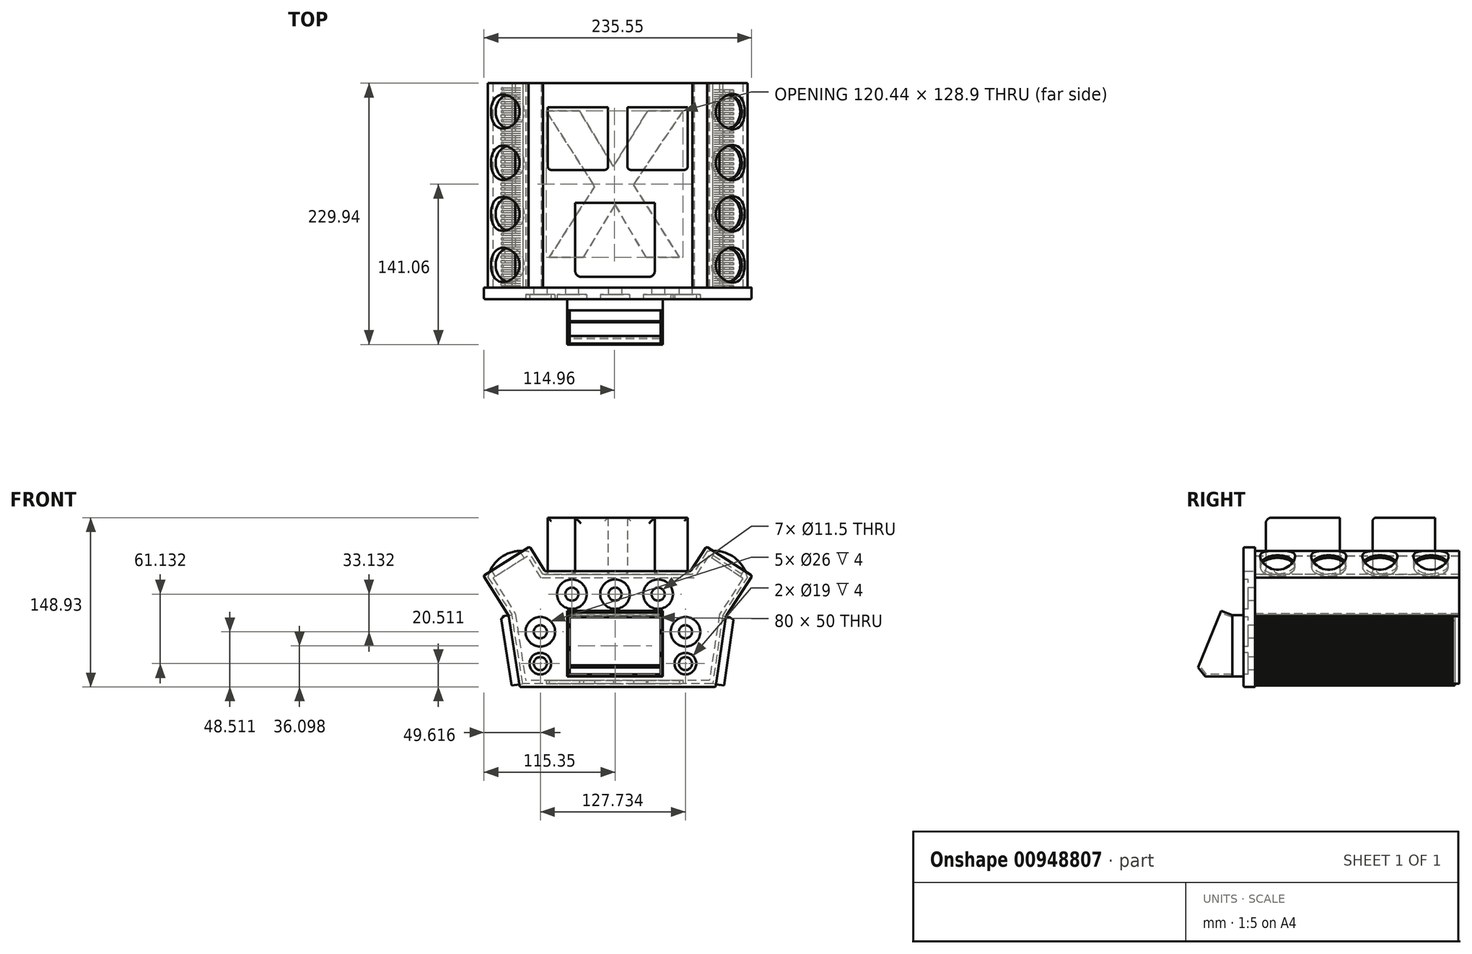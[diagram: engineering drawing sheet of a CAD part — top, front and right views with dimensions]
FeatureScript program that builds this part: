
annotation { "Feature Type Name" : "Feature", "Feature Type Description" : "" }
export const myFeature = defineFeature(function(context is Context, id is Id, definition is map)
    precondition{}
    {
        {
            var Q0;
            Q0=qCreatedBy(makeId("Front.planeOp"),FACE);
            var sketch = newSketch(context, id + "F0", { "sketchPlane" : qUnion([Q0])});
            skPoint(sketch, "E0.middle", {"position": v(0, 0) * mm});
            skLineSegment(sketch, "E1", {"start": v(-83.79, -31.42) * mm, "end": v(-93.51, 30.9) * mm});
            skLineSegment(sketch, "E2", {"start": v(-93.51, 30.9) * mm, "end": v(-115.73, 66.29) * mm});
            skLineSegment(sketch, "E3", {"start": v(-115.73, 66.29) * mm, "end": v(-75.07, 91.8) * mm});
            skLineSegment(sketch, "E4", {"start": v(-75.07, 91.8) * mm, "end": v(-61.7, 70.51) * mm});
            skLineSegment(sketch, "E5", {"start": v(-61.7, 70.51) * mm, "end": v(66.57, 70.51) * mm});
            skLineSegment(sketch, "E6", {"start": v(-83.79, -31.42) * mm, "end": v(66.57, -31.42) * mm});
            skLineSegment(sketch, "E7", {"start": v(66.57, -31.42) * mm, "end": v(88.65, -31.42) * mm});
            skLineSegment(sketch, "E8", {"start": v(97.66, 30.9) * mm, "end": v(88.65, -31.42) * mm});
            skLineSegment(sketch, "E9", {"start": v(120.6, 66.29) * mm, "end": v(97.66, 30.9) * mm});
            skLineSegment(sketch, "E10", {"start": v(80.44, 91.8) * mm, "end": v(120.6, 66.29) * mm});
            skLineSegment(sketch, "E11", {"start": v(80.44, 91.8) * mm, "end": v(66.57, 70.51) * mm});
            skSolve(sketch);
        }
        {
            var Q0;
            Q0 = qSketchRegion(id + "F0", true);
            extrude(context, id + "F1", {"entities" : qUnion([Q0]), "depth" : 10 * mm, "offsetDistance" : 25 * mm});
        }
        {
            var Q0;
            Q0=makeQuery(id+"F1.opExtrude","CAP_FACE",FACE,{"disambiguationData":[OSD([sQuery(id+"F0.wireOp",EDGE,"E1"),sQuery(id+"F0.wireOp",EDGE,"E2"),sQuery(id+"F0.wireOp",EDGE,"E3"),sQuery(id+"F0.wireOp",EDGE,"E4"),sQuery(id+"F0.wireOp",EDGE,"E5"),sQuery(id+"F0.wireOp",EDGE,"E6"),sQuery(id+"F0.wireOp",EDGE,"E7"),sQuery(id+"F0.wireOp",EDGE,"E8"),sQuery(id+"F0.wireOp",EDGE,"E9"),sQuery(id+"F0.wireOp",EDGE,"E10"),sQuery(id+"F0.wireOp",EDGE,"E11")])],"isStart":true});
            var sketch = newSketch(context, id + "F2", { "sketchPlane" : qUnion([Q0])});
            skLineSegment(sketch, "E12", {"start": v(-94.63, 30.9) * mm, "end": v(-86.01, -28.73) * mm});
            skPoint(sketch, "E13.startSnap0", {"position": v(-109.12, 48.59) * mm});
            skLineSegment(sketch, "E14", {"start": v(-81.1, 87.8) * mm, "end": v(-68.2, 67.51) * mm});
            skLineSegment(sketch, "E15", {"start": v(-69.82, 64.51) * mm, "end": v(65.02, 64.51) * mm});
            skLineSegment(sketch, "E16", {"start": v(63.36, 67.51) * mm, "end": v(76.02, 87.67) * mm});
            skLineSegment(sketch, "E17", {"start": v(65.02, 64.51) * mm, "end": v(76.96, 83.53) * mm});
            skLineSegment(sketch, "E18", {"start": v(-68.2, 67.51) * mm, "end": v(63.36, 67.51) * mm});
            skLineSegment(sketch, "E19", {"start": v(76.96, 83.53) * mm, "end": v(107.45, 64.4) * mm});
            skLineSegment(sketch, "E20", {"start": v(107.45, 64.4) * mm, "end": v(87.77, 33.03) * mm});
            skLineSegment(sketch, "E21", {"start": v(81.21, -28.68) * mm, "end": v(90.64, 31.96) * mm});
            skLineSegment(sketch, "E22", {"start": v(-83.06, -25.73) * mm, "end": v(78.64, -25.73) * mm});
            skLineSegment(sketch, "E23", {"start": v(87.77, 33.03) * mm, "end": v(78.64, -25.73) * mm});
            skLineSegment(sketch, "E24", {"start": v(-91.98, 32.32) * mm, "end": v(-83.06, -25.73) * mm});
            skLineSegment(sketch, "E25", {"start": v(-86.01, -28.73) * mm, "end": v(81.21, -28.68) * mm});
            skLineSegment(sketch, "E26", {"start": v(-112.62, 64.18) * mm, "end": v(-91.98, 32.32) * mm});
            skLineSegment(sketch, "E27", {"start": v(-112.62, 64.18) * mm, "end": v(-82.37, 83.78) * mm});
            skLineSegment(sketch, "E28", {"start": v(-82.37, 83.78) * mm, "end": v(-69.82, 64.51) * mm});
            skLineSegment(sketch, "E29", {"start": v(-94.63, 30.9) * mm, "end": v(-116.6, 64.8) * mm});
            skLineSegment(sketch, "E30", {"start": v(-116.6, 64.8) * mm, "end": v(-81.1, 87.8) * mm});
            skArc(sketch, "E31", {"start": v(-81.1, 87.8) * mm, "mid": v(-103.53, 83.54) * mm, "end": v(-116.6, 64.8) * mm});
            skArc(sketch, "E32", {"start": v(111.87, 65.21) * mm, "mid": v(98.52, 83.74) * mm, "end": v(76.02, 87.67) * mm});
            skLineSegment(sketch, "E33", {"start": v(76.02, 87.67) * mm, "end": v(111.87, 65.21) * mm});
            skLineSegment(sketch, "E34", {"start": v(111.87, 65.21) * mm, "end": v(90.64, 31.96) * mm});
            skSolve(sketch);
        }
        {
            var Q0;
            Q0=makeQuery(id+"F2.imprint","IMPRINT",FACE,{"disambiguationData":[TD([[makeQuery(id+"F2.imprint","IMPRINT",EDGE,{"derivedFrom":sQuery(id+"F2.wireOp",EDGE,"E12")}),1.0]])]});
            extrude(context, id + "F3", {"entities" : qUnion([Q0]), "operationType" : NewBodyOperationType.ADD, "depth" : 180 * mm, "offsetDistance" : 25 * mm});
        }
        {
            var Q0;
            Q0=makeQuery(id+"F1.opExtrude","CAP_FACE",FACE,{"disambiguationData":[OSD([sQuery(id+"F0.wireOp",EDGE,"E1"),sQuery(id+"F0.wireOp",EDGE,"E2"),sQuery(id+"F0.wireOp",EDGE,"E3"),sQuery(id+"F0.wireOp",EDGE,"E4"),sQuery(id+"F0.wireOp",EDGE,"E5"),sQuery(id+"F0.wireOp",EDGE,"E6"),sQuery(id+"F0.wireOp",EDGE,"E7"),sQuery(id+"F0.wireOp",EDGE,"E8"),sQuery(id+"F0.wireOp",EDGE,"E9"),sQuery(id+"F0.wireOp",EDGE,"E10"),sQuery(id+"F0.wireOp",EDGE,"E11")])],"isStart":false});
            var sketch = newSketch(context, id + "F4", { "sketchPlane" : qUnion([Q0])});
            skPoint(sketch, "E35.middle", {"position": v(0, 0) * mm});
            skLineSegment(sketch, "E36", {"start": v(0, -22.32) * mm, "end": v(-42, -22.32) * mm});
            skLineSegment(sketch, "E37", {"start": v(42, -22.32) * mm, "end": v(0, -22.32) * mm});
            skLineSegment(sketch, "E38", {"start": v(-42, -22.32) * mm, "end": v(-42, 31.68) * mm});
            skLineSegment(sketch, "E39", {"start": v(42, -22.32) * mm, "end": v(42, 31.68) * mm});
            skLineSegment(sketch, "E40", {"start": v(-42, 31.68) * mm, "end": v(42, 31.68) * mm});
            skLineSegment(sketch, "E41", {"start": v(-40, 31.68) * mm, "end": v(-39.18, 31.68) * mm});
            skLineSegment(sketch, "E42", {"start": v(-35.27, 29.68) * mm, "end": v(-40, 29.68) * mm});
            skLineSegment(sketch, "E43", {"start": v(42, 16.04) * mm, "end": v(40, 16.04) * mm});
            skLineSegment(sketch, "E44", {"start": v(40, 16.04) * mm, "end": v(40, 29.68) * mm});
            skLineSegment(sketch, "E45", {"start": v(-30.6, -22.32) * mm, "end": v(-30.6, -20.32) * mm});
            skLineSegment(sketch, "E46", {"start": v(-30.6, -20.32) * mm, "end": v(-40, -20.32) * mm});
            skLineSegment(sketch, "E47", {"start": v(-40, -20.32) * mm, "end": v(-39.67, -20.32) * mm});
            skLineSegment(sketch, "E48", {"start": v(-40, -20.32) * mm, "end": v(-40, 29.68) * mm});
            skLineSegment(sketch, "E49", {"start": v(40, 29.68) * mm, "end": v(-35.27, 29.68) * mm});
            skLineSegment(sketch, "E50", {"start": v(40, 16.04) * mm, "end": v(40, -20.32) * mm});
            skLineSegment(sketch, "E51", {"start": v(40, -20.32) * mm, "end": v(-30.6, -20.32) * mm});
            skSolve(sketch);
        }
        {
            var Q0;
            Q0 = qSketchRegion(id + "F4", true);
            var Q1;
            Q1=sQuery(id+"F4.wireOp",EDGE,"E39");
            var Q2;
            Q2=sQuery(id+"F4.wireOp",EDGE,"E40");
            var Q3;
            Q3=sQuery(id+"F4.wireOp",EDGE,"E49");
            var Q4;
            Q4=sQuery(id+"F4.wireOp",EDGE,"E44");
            var Q5;
            Q5=sQuery(id+"F4.wireOp",EDGE,"E50");
            var Q6;
            Q6=sQuery(id+"F4.wireOp",EDGE,"E51");
            var Q7;
            Q7=sQuery(id+"F4.wireOp",EDGE,"E48");
            var Q8;
            Q8=sQuery(id+"F4.wireOp",EDGE,"E46");
            var Q9;
            Q9=sQuery(id+"F4.wireOp",EDGE,"E38");
            var Q10;
            Q10=sQuery(id+"F4.wireOp",EDGE,"E42");
            extrude(context, id + "F5", {"entities" : qUnion([Q0]), "operationType" : NewBodyOperationType.ADD, "surfaceOperationType" : NewSurfaceOperationType.ADD, "surfaceEntities" : qUnion([Q1, Q2, Q3, Q4, Q5, Q6, Q7, Q8, Q9, Q10]), "depth" : 10 * mm, "offsetDistance" : 25 * mm});
        }
        {
            var Q0;
            Q0=makeQuery(id+"F3.opExtrude","SWEPT_FACE",FACE,{"disambiguationData":[OSD([sQuery(id+"F2.wireOp",EDGE,"E30")])]});
            var sketch = newSketch(context, id + "F6", { "sketchPlane" : qUnion([Q0])});
            skPoint(sketch, "E52.endSnap0", {"position": v(41.46, 0) * mm});
            skCircle(sketch, "E53", {"center": v(41.61, 20) * mm, "radius": 15 * mm});
            skCircle(sketch, "E54", {"center": v(41.61, 65) * mm, "radius": 15 * mm});
            skCircle(sketch, "E55", {"center": v(41.61, 110) * mm, "radius": 15 * mm});
            skCircle(sketch, "E56", {"center": v(41.61, 155) * mm, "radius": 15 * mm});
            skSolve(sketch);
        }
        {
            var Q0;
            Q0=makeQuery(id+"F3.opExtrude","SWEPT_FACE",FACE,{"disambiguationData":[OSD([sQuery(id+"F2.wireOp",EDGE,"E33")])]});
            var sketch = newSketch(context, id + "F7", { "sketchPlane" : qUnion([Q0])});
            skCircle(sketch, "E57", {"center": v(-39.2, 20) * mm, "radius": 15 * mm});
            skCircle(sketch, "E58", {"center": v(-39.2, 65) * mm, "radius": 15 * mm});
            skCircle(sketch, "E59", {"center": v(-39.2, 110) * mm, "radius": 15 * mm});
            skCircle(sketch, "E60", {"center": v(-39.2, 155) * mm, "radius": 15 * mm});
            skSolve(sketch);
        }
        {
            var Q0;
            {var subQ0=sQuery(id+"F2.wireOp",EDGE,"E33");Q0=makeQuery(id+"F2.imprint","IMPRINT",FACE,{"disambiguationData":[TD([[makeQuery(id+"F2.imprint","IMPRINT",EDGE,{"derivedFrom":subQ0}),1.0]])]});}
            var Q1;
            {var subQ0=sQuery(id+"F2.wireOp",EDGE,"E32");var subQ1=makeQuery(id+"F1.opExtrude","CAP_EDGE",EDGE,{"disambiguationData":[OSD([sQuery(id+"F0.wireOp",EDGE,"E3")])],"isStart":true});var subQ2=makeQuery(id+"F2.imprint","INTERSECT",VERTEX,{"disambiguationData":[OD(0.0)],"derivedFrom":[subQ1,subQ0]});Q1=makeQuery(id+"F2.imprint","IMPRINT",FACE,{"disambiguationData":[TD([[makeQuery(id+"F2.imprint","IMPRINT",EDGE,{"disambiguationData":[TD([[subQ2,-1.0]])],"derivedFrom":subQ0}),1.0]])]});}
            var Q2;
            {var subQ0=sQuery(id+"F2.wireOp",EDGE,"E31");var subQ1=makeQuery(id+"F1.opExtrude","CAP_EDGE",EDGE,{"disambiguationData":[OSD([sQuery(id+"F0.wireOp",EDGE,"E10")])],"isStart":true});var subQ2=makeQuery(id+"F2.imprint","INTERSECT",VERTEX,{"disambiguationData":[OD(0.0)],"derivedFrom":[subQ1,subQ0]});Q2=makeQuery(id+"F2.imprint","IMPRINT",FACE,{"disambiguationData":[TD([[makeQuery(id+"F2.imprint","IMPRINT",EDGE,{"disambiguationData":[TD([[subQ2,-1.0]])],"derivedFrom":subQ0}),1.0]])]});}
            var Q3;
            {var subQ0=sQuery(id+"F2.wireOp",EDGE,"E30");Q3=makeQuery(id+"F2.imprint","IMPRINT",FACE,{"disambiguationData":[TD([[makeQuery(id+"F2.imprint","IMPRINT",EDGE,{"derivedFrom":subQ0}),1.0]])]});}
            extrude(context, id + "F8", {"entities" : qUnion([Q0, Q1, Q2, Q3]), "operationType" : NewBodyOperationType.ADD, "depth" : 180 * mm, "offsetDistance" : 25 * mm});
        }
        {
            var Q0;
            Q0 = qSketchRegion(id + "F6", true);
            extrude(context, id + "F9", {"entities" : qUnion([Q0]), "operationType" : NewBodyOperationType.REMOVE, "oppositeDirection" : true, "depth" : 20 * mm, "offsetDistance" : 25 * mm, "hasDraft" : true, "draftAngle" : 3 * degree, "symmetric" : true});
        }
        {
            var Q0;
            Q0 = qSketchRegion(id + "F7", true);
            extrude(context, id + "F10", {"entities" : qUnion([Q0]), "operationType" : NewBodyOperationType.REMOVE, "oppositeDirection" : true, "depth" : 25 * mm, "offsetDistance" : 25 * mm, "symmetric" : true});
        }
        {
            var Q0;
            Q0=makeQuery(id+"F1.opExtrude","CAP_EDGE",EDGE,{"disambiguationData":[OSD([sQuery(id+"F0.wireOp",EDGE,"E5")])],"isStart":false});
            var Q1;
            Q1=makeQuery(id+"F1.opExtrude","CAP_EDGE",EDGE,{"disambiguationData":[OSD([sQuery(id+"F0.wireOp",EDGE,"E10")])],"isStart":false});
            var Q2;
            Q2=makeQuery(id+"F1.opExtrude","CAP_EDGE",EDGE,{"disambiguationData":[OSD([sQuery(id+"F0.wireOp",EDGE,"E11")])],"isStart":false});
            var Q3;
            Q3=makeQuery(id+"F1.opExtrude","CAP_EDGE",EDGE,{"disambiguationData":[OSD([sQuery(id+"F0.wireOp",EDGE,"E9")])],"isStart":false});
            var Q4;
            Q4=makeQuery(id+"F1.opExtrude","CAP_EDGE",EDGE,{"disambiguationData":[OSD([sQuery(id+"F0.wireOp",EDGE,"E8")])],"isStart":false});
            var Q5;
            Q5=makeQuery(id+"F1.opExtrude","CAP_EDGE",EDGE,{"disambiguationData":[OSD([sQuery(id+"F0.wireOp",EDGE,"E6"),sQuery(id+"F0.wireOp",EDGE,"E7")])],"isStart":false});
            var Q6;
            Q6=makeQuery(id+"F1.opExtrude","CAP_EDGE",EDGE,{"disambiguationData":[OSD([sQuery(id+"F0.wireOp",EDGE,"E1")])],"isStart":false});
            var Q7;
            Q7=makeQuery(id+"F1.opExtrude","CAP_EDGE",EDGE,{"disambiguationData":[OSD([sQuery(id+"F0.wireOp",EDGE,"E2")])],"isStart":false});
            var Q8;
            Q8=makeQuery(id+"F1.opExtrude","CAP_EDGE",EDGE,{"disambiguationData":[OSD([sQuery(id+"F0.wireOp",EDGE,"E3")])],"isStart":false});
            var Q9;
            Q9=makeQuery(id+"F1.opExtrude","CAP_EDGE",EDGE,{"disambiguationData":[OSD([sQuery(id+"F0.wireOp",EDGE,"E4")])],"isStart":false});
            var Q10;
            Q10=makeQuery(id+"F1.opExtrude","SWEPT_EDGE",EDGE,{"disambiguationData":[OSD([sQuery(id+"F0.wireOp",EDGE,"E3"),sQuery(id+"F0.wireOp",EDGE,"E4")])]});
            var Q11;
            Q11=makeQuery(id+"F1.opExtrude","SWEPT_EDGE",EDGE,{"disambiguationData":[OSD([sQuery(id+"F0.wireOp",EDGE,"E4"),sQuery(id+"F0.wireOp",EDGE,"E5")])]});
            var Q12;
            Q12=makeQuery(id+"F1.opExtrude","SWEPT_EDGE",EDGE,{"disambiguationData":[OSD([sQuery(id+"F0.wireOp",EDGE,"E2"),sQuery(id+"F0.wireOp",EDGE,"E3")])]});
            var Q13;
            Q13=makeQuery(id+"F1.opExtrude","SWEPT_EDGE",EDGE,{"disambiguationData":[OSD([sQuery(id+"F0.wireOp",EDGE,"E1"),sQuery(id+"F0.wireOp",EDGE,"E2")])]});
            var Q14;
            Q14=makeQuery(id+"F1.opExtrude","SWEPT_EDGE",EDGE,{"disambiguationData":[OSD([sQuery(id+"F0.wireOp",EDGE,"E1"),sQuery(id+"F0.wireOp",EDGE,"E6")])]});
            var Q15;
            Q15=makeQuery(id+"F1.opExtrude","SWEPT_EDGE",EDGE,{"disambiguationData":[OSD([sQuery(id+"F0.wireOp",EDGE,"E7"),sQuery(id+"F0.wireOp",EDGE,"E8")])]});
            var Q16;
            Q16=makeQuery(id+"F1.opExtrude","SWEPT_EDGE",EDGE,{"disambiguationData":[OSD([sQuery(id+"F0.wireOp",EDGE,"E8"),sQuery(id+"F0.wireOp",EDGE,"E9")])]});
            var Q17;
            Q17=makeQuery(id+"F1.opExtrude","SWEPT_EDGE",EDGE,{"disambiguationData":[OSD([sQuery(id+"F0.wireOp",EDGE,"E9"),sQuery(id+"F0.wireOp",EDGE,"E10")])]});
            var Q18;
            Q18=makeQuery(id+"F1.opExtrude","SWEPT_EDGE",EDGE,{"disambiguationData":[OSD([sQuery(id+"F0.wireOp",EDGE,"E10"),sQuery(id+"F0.wireOp",EDGE,"E11")])]});
            var Q19;
            Q19=makeQuery(id+"F1.opExtrude","SWEPT_EDGE",EDGE,{"disambiguationData":[OSD([sQuery(id+"F0.wireOp",EDGE,"E5"),sQuery(id+"F0.wireOp",EDGE,"E11")])]});
            fillet(context, id + "F11", {"entities" : qUnion([Q0, Q1, Q2, Q3, Q4, Q5, Q6, Q7, Q8, Q9, Q10, Q11, Q12, Q13, Q14, Q15, Q16, Q17, Q18, Q19]), "radius" : 1 * mm, "tangentPropagation" : true, "allowEdgeOverflow" : false});
        }
        {
            var Q0;
            Q0=makeQuery(id+"F5.boolean.opBoolean","SPLIT",FACE,{"disambiguationData":[TD([makeQuery(id+"F5.opExtrude","SWEPT_FACE",FACE,{"disambiguationData":[OSD([sQuery(id+"F4.wireOp",EDGE,"E48")])]})])],"derivedFrom":makeQuery(id+"F1.opExtrude","CAP_FACE",FACE,{"disambiguationData":[OSD([sQuery(id+"F0.wireOp",EDGE,"E1"),sQuery(id+"F0.wireOp",EDGE,"E2"),sQuery(id+"F0.wireOp",EDGE,"E3"),sQuery(id+"F0.wireOp",EDGE,"E4"),sQuery(id+"F0.wireOp",EDGE,"E5"),sQuery(id+"F0.wireOp",EDGE,"E6"),sQuery(id+"F0.wireOp",EDGE,"E7"),sQuery(id+"F0.wireOp",EDGE,"E8"),sQuery(id+"F0.wireOp",EDGE,"E9"),sQuery(id+"F0.wireOp",EDGE,"E10"),sQuery(id+"F0.wireOp",EDGE,"E11")])],"isStart":false})});
            extrude(context, id + "F12", {"entities" : qUnion([Q0]), "operationType" : NewBodyOperationType.REMOVE, "oppositeDirection" : true, "depth" : 25 * mm, "offsetDistance" : 25 * mm});
        }
        {
            var Q0;
            Q0=makeQuery(id+"F3.opExtrude","SWEPT_FACE",FACE,{"disambiguationData":[OSD([sQuery(id+"F2.wireOp",EDGE,"E21")])]});
            var sketch = newSketch(context, id + "F13", { "sketchPlane" : qUnion([Q0])});
            skLineSegment(sketch, "E61.bottom", {"start": v(0, 45.5) * mm, "end": v(-2, 45.5) * mm});
            skLineSegment(sketch, "E61.top", {"start": v(0, -15.87) * mm, "end": v(-2, -15.87) * mm});
            skLineSegment(sketch, "E61.left", {"start": v(0, 45.5) * mm, "end": v(0, -15.87) * mm});
            skLineSegment(sketch, "E61.right", {"start": v(-2, 45.5) * mm, "end": v(-2, -15.87) * mm});
            skLineSegment(sketch, "E62.bottom", {"start": v(-4, 45.5) * mm, "end": v(-6, 45.5) * mm});
            skLineSegment(sketch, "E62.top", {"start": v(-4, -15.87) * mm, "end": v(-6, -15.87) * mm});
            skLineSegment(sketch, "E62.left", {"start": v(-4, 45.5) * mm, "end": v(-4, -15.87) * mm});
            skLineSegment(sketch, "E62.right", {"start": v(-6, 45.5) * mm, "end": v(-6, -15.87) * mm});
            skLineSegment(sketch, "E63.right", {"start": v(-8, 45.5) * mm, "end": v(-8, -15.87) * mm});
            skLineSegment(sketch, "E64.bottom", {"start": v(-10, 45.5) * mm, "end": v(-12, 45.5) * mm});
            skLineSegment(sketch, "E64.top", {"start": v(-10, -15.87) * mm, "end": v(-12, -15.87) * mm});
            skLineSegment(sketch, "E64.left", {"start": v(-10, 45.5) * mm, "end": v(-10, -15.87) * mm});
            skLineSegment(sketch, "E64.right", {"start": v(-12, 45.5) * mm, "end": v(-12, -15.87) * mm});
            skLineSegment(sketch, "E65.bottom", {"start": v(-14, 45.5) * mm, "end": v(-16, 45.5) * mm});
            skLineSegment(sketch, "E65.top", {"start": v(-14, -15.87) * mm, "end": v(-16, -15.87) * mm});
            skLineSegment(sketch, "E65.left", {"start": v(-14, 45.5) * mm, "end": v(-14, -15.87) * mm});
            skLineSegment(sketch, "E65.right", {"start": v(-16, 45.5) * mm, "end": v(-16, -15.87) * mm});
            skLineSegment(sketch, "E66.bottom", {"start": v(-18, 45.5) * mm, "end": v(-20, 45.5) * mm});
            skLineSegment(sketch, "E66.top", {"start": v(-18, -15.87) * mm, "end": v(-20, -15.87) * mm});
            skLineSegment(sketch, "E66.left", {"start": v(-18, 45.5) * mm, "end": v(-18, -15.87) * mm});
            skLineSegment(sketch, "E66.right", {"start": v(-20, 45.5) * mm, "end": v(-20, -15.87) * mm});
            skLineSegment(sketch, "E67.right", {"start": v(-22, 45.5) * mm, "end": v(-22, -15.87) * mm});
            skLineSegment(sketch, "E68.bottom", {"start": v(-24, 45.5) * mm, "end": v(-26, 45.5) * mm});
            skLineSegment(sketch, "E68.top", {"start": v(-24, -15.87) * mm, "end": v(-26, -15.87) * mm});
            skLineSegment(sketch, "E68.left", {"start": v(-24, 45.5) * mm, "end": v(-24, -15.87) * mm});
            skLineSegment(sketch, "E68.right", {"start": v(-26, 45.5) * mm, "end": v(-26, -15.87) * mm});
            skLineSegment(sketch, "E69.bottom", {"start": v(-28, 45.5) * mm, "end": v(-30, 45.5) * mm});
            skLineSegment(sketch, "E69.top", {"start": v(-28, -15.87) * mm, "end": v(-30, -15.87) * mm});
            skLineSegment(sketch, "E69.left", {"start": v(-28, 45.5) * mm, "end": v(-28, -15.87) * mm});
            skLineSegment(sketch, "E69.right", {"start": v(-30, 45.5) * mm, "end": v(-30, -15.87) * mm});
            skLineSegment(sketch, "E70.bottom", {"start": v(-32, 45.5) * mm, "end": v(-34, 45.5) * mm});
            skLineSegment(sketch, "E70.top", {"start": v(-32, -15.87) * mm, "end": v(-34, -15.87) * mm});
            skLineSegment(sketch, "E70.left", {"start": v(-32, 45.5) * mm, "end": v(-32, -15.87) * mm});
            skLineSegment(sketch, "E70.right", {"start": v(-34, 45.5) * mm, "end": v(-34, -15.87) * mm});
            skLineSegment(sketch, "E71.right", {"start": v(-36, 45.5) * mm, "end": v(-36, -15.87) * mm});
            skLineSegment(sketch, "E72.bottom", {"start": v(-38, 45.5) * mm, "end": v(-40, 45.5) * mm});
            skLineSegment(sketch, "E72.top", {"start": v(-38, -15.87) * mm, "end": v(-40, -15.87) * mm});
            skLineSegment(sketch, "E72.left", {"start": v(-38, 45.5) * mm, "end": v(-38, -15.87) * mm});
            skLineSegment(sketch, "E72.right", {"start": v(-40, 45.5) * mm, "end": v(-40, -15.87) * mm});
            skLineSegment(sketch, "E73.bottom", {"start": v(-42, 45.5) * mm, "end": v(-44, 45.5) * mm});
            skLineSegment(sketch, "E73.top", {"start": v(-42, -15.87) * mm, "end": v(-44, -15.87) * mm});
            skLineSegment(sketch, "E73.left", {"start": v(-42, 45.5) * mm, "end": v(-42, -15.87) * mm});
            skLineSegment(sketch, "E73.right", {"start": v(-44, 45.5) * mm, "end": v(-44, -15.87) * mm});
            skLineSegment(sketch, "E74.bottom", {"start": v(-46, 45.5) * mm, "end": v(-48, 45.5) * mm});
            skLineSegment(sketch, "E74.top", {"start": v(-46, -15.87) * mm, "end": v(-48, -15.87) * mm});
            skLineSegment(sketch, "E74.left", {"start": v(-46, 45.5) * mm, "end": v(-46, -15.87) * mm});
            skLineSegment(sketch, "E74.right", {"start": v(-48, 45.5) * mm, "end": v(-48, -15.87) * mm});
            skLineSegment(sketch, "E75.right", {"start": v(-50, 45.5) * mm, "end": v(-50, -15.87) * mm});
            skLineSegment(sketch, "E76.bottom", {"start": v(-52, 45.5) * mm, "end": v(-54, 45.5) * mm});
            skLineSegment(sketch, "E76.top", {"start": v(-52, -15.87) * mm, "end": v(-54, -15.87) * mm});
            skLineSegment(sketch, "E76.left", {"start": v(-52, 45.5) * mm, "end": v(-52, -15.87) * mm});
            skLineSegment(sketch, "E76.right", {"start": v(-54, 45.5) * mm, "end": v(-54, -15.87) * mm});
            skLineSegment(sketch, "E77.bottom", {"start": v(-56, 45.5) * mm, "end": v(-58, 45.5) * mm});
            skLineSegment(sketch, "E77.top", {"start": v(-56, -15.87) * mm, "end": v(-58, -15.87) * mm});
            skLineSegment(sketch, "E77.left", {"start": v(-56, 45.5) * mm, "end": v(-56, -15.87) * mm});
            skLineSegment(sketch, "E77.right", {"start": v(-58, 45.5) * mm, "end": v(-58, -15.87) * mm});
            skLineSegment(sketch, "E78.bottom", {"start": v(-60, 45.5) * mm, "end": v(-62, 45.5) * mm});
            skLineSegment(sketch, "E78.top", {"start": v(-60, -15.87) * mm, "end": v(-62, -15.87) * mm});
            skLineSegment(sketch, "E78.left", {"start": v(-60, 45.5) * mm, "end": v(-60, -15.87) * mm});
            skLineSegment(sketch, "E78.right", {"start": v(-62, 45.5) * mm, "end": v(-62, -15.87) * mm});
            skLineSegment(sketch, "E79.right", {"start": v(-64, 45.5) * mm, "end": v(-64, -15.87) * mm});
            skLineSegment(sketch, "E80.bottom", {"start": v(-66, 45.5) * mm, "end": v(-68, 45.5) * mm});
            skLineSegment(sketch, "E80.top", {"start": v(-66, -15.87) * mm, "end": v(-68, -15.87) * mm});
            skLineSegment(sketch, "E80.left", {"start": v(-66, 45.5) * mm, "end": v(-66, -15.87) * mm});
            skLineSegment(sketch, "E80.right", {"start": v(-68, 45.5) * mm, "end": v(-68, -15.87) * mm});
            skLineSegment(sketch, "E81.bottom", {"start": v(-70, 45.5) * mm, "end": v(-72, 45.5) * mm});
            skLineSegment(sketch, "E81.top", {"start": v(-70, -15.87) * mm, "end": v(-72, -15.87) * mm});
            skLineSegment(sketch, "E81.left", {"start": v(-70, 45.5) * mm, "end": v(-70, -15.87) * mm});
            skLineSegment(sketch, "E81.right", {"start": v(-72, 45.5) * mm, "end": v(-72, -15.87) * mm});
            skLineSegment(sketch, "E82.bottom", {"start": v(-74, 45.5) * mm, "end": v(-76, 45.5) * mm});
            skLineSegment(sketch, "E82.top", {"start": v(-74, -15.87) * mm, "end": v(-76, -15.87) * mm});
            skLineSegment(sketch, "E82.left", {"start": v(-74, 45.5) * mm, "end": v(-74, -15.87) * mm});
            skLineSegment(sketch, "E82.right", {"start": v(-76, 45.5) * mm, "end": v(-76, -15.87) * mm});
            skLineSegment(sketch, "E83.right", {"start": v(-78, 45.5) * mm, "end": v(-78, -15.87) * mm});
            skLineSegment(sketch, "E84.bottom", {"start": v(-80, 45.5) * mm, "end": v(-82, 45.5) * mm});
            skLineSegment(sketch, "E84.top", {"start": v(-80, -15.87) * mm, "end": v(-82, -15.87) * mm});
            skLineSegment(sketch, "E84.left", {"start": v(-80, 45.5) * mm, "end": v(-80, -15.87) * mm});
            skLineSegment(sketch, "E84.right", {"start": v(-82, 45.5) * mm, "end": v(-82, -15.87) * mm});
            skLineSegment(sketch, "E85.bottom", {"start": v(-84, 45.5) * mm, "end": v(-86, 45.5) * mm});
            skLineSegment(sketch, "E85.top", {"start": v(-84, -15.87) * mm, "end": v(-86, -15.87) * mm});
            skLineSegment(sketch, "E85.left", {"start": v(-84, 45.5) * mm, "end": v(-84, -15.87) * mm});
            skLineSegment(sketch, "E85.right", {"start": v(-86, 45.5) * mm, "end": v(-86, -15.87) * mm});
            skLineSegment(sketch, "E86.bottom", {"start": v(-88, 45.5) * mm, "end": v(-90, 45.5) * mm});
            skLineSegment(sketch, "E86.top", {"start": v(-88, -15.87) * mm, "end": v(-90, -15.87) * mm});
            skLineSegment(sketch, "E86.left", {"start": v(-88, 45.5) * mm, "end": v(-88, -15.87) * mm});
            skLineSegment(sketch, "E86.right", {"start": v(-90, 45.5) * mm, "end": v(-90, -15.87) * mm});
            skLineSegment(sketch, "E87.right", {"start": v(-92, 45.5) * mm, "end": v(-92, -15.87) * mm});
            skLineSegment(sketch, "E88.bottom", {"start": v(-94, 45.5) * mm, "end": v(-96, 45.5) * mm});
            skLineSegment(sketch, "E88.top", {"start": v(-94, -15.87) * mm, "end": v(-96, -15.87) * mm});
            skLineSegment(sketch, "E88.left", {"start": v(-94, 45.5) * mm, "end": v(-94, -15.87) * mm});
            skLineSegment(sketch, "E88.right", {"start": v(-96, 45.5) * mm, "end": v(-96, -15.87) * mm});
            skLineSegment(sketch, "E89.bottom", {"start": v(-98, 45.5) * mm, "end": v(-100, 45.5) * mm});
            skLineSegment(sketch, "E89.top", {"start": v(-98, -15.87) * mm, "end": v(-100, -15.87) * mm});
            skLineSegment(sketch, "E89.left", {"start": v(-98, 45.5) * mm, "end": v(-98, -15.87) * mm});
            skLineSegment(sketch, "E89.right", {"start": v(-100, 45.5) * mm, "end": v(-100, -15.87) * mm});
            skLineSegment(sketch, "E90.bottom", {"start": v(-102, 45.5) * mm, "end": v(-104, 45.5) * mm});
            skLineSegment(sketch, "E90.top", {"start": v(-102, -15.87) * mm, "end": v(-104, -15.87) * mm});
            skLineSegment(sketch, "E90.left", {"start": v(-102, 45.5) * mm, "end": v(-102, -15.87) * mm});
            skLineSegment(sketch, "E90.right", {"start": v(-104, 45.5) * mm, "end": v(-104, -15.87) * mm});
            skLineSegment(sketch, "E91.right", {"start": v(-106, 45.5) * mm, "end": v(-106, -15.87) * mm});
            skLineSegment(sketch, "E92.bottom", {"start": v(-108, 45.5) * mm, "end": v(-110, 45.5) * mm});
            skLineSegment(sketch, "E92.top", {"start": v(-108, -15.87) * mm, "end": v(-110, -15.87) * mm});
            skLineSegment(sketch, "E92.left", {"start": v(-108, 45.5) * mm, "end": v(-108, -15.87) * mm});
            skLineSegment(sketch, "E92.right", {"start": v(-110, 45.5) * mm, "end": v(-110, -15.87) * mm});
            skLineSegment(sketch, "E93.bottom", {"start": v(-112, 45.5) * mm, "end": v(-114, 45.5) * mm});
            skLineSegment(sketch, "E93.top", {"start": v(-112, -15.87) * mm, "end": v(-114, -15.87) * mm});
            skLineSegment(sketch, "E93.left", {"start": v(-112, 45.5) * mm, "end": v(-112, -15.87) * mm});
            skLineSegment(sketch, "E93.right", {"start": v(-114, 45.5) * mm, "end": v(-114, -15.87) * mm});
            skLineSegment(sketch, "E94.right", {"start": v(-116, 45.5) * mm, "end": v(-116, -15.87) * mm});
            skLineSegment(sketch, "E95.bottom", {"start": v(-118, 45.5) * mm, "end": v(-120, 45.5) * mm});
            skLineSegment(sketch, "E95.top", {"start": v(-118, -15.87) * mm, "end": v(-120, -15.87) * mm});
            skLineSegment(sketch, "E95.left", {"start": v(-118, 45.5) * mm, "end": v(-118, -15.87) * mm});
            skLineSegment(sketch, "E95.right", {"start": v(-120, 45.5) * mm, "end": v(-120, -15.87) * mm});
            skLineSegment(sketch, "E96.bottom", {"start": v(-122, 45.5) * mm, "end": v(-124, 45.5) * mm});
            skLineSegment(sketch, "E96.top", {"start": v(-122, -15.87) * mm, "end": v(-124, -15.87) * mm});
            skLineSegment(sketch, "E96.left", {"start": v(-122, 45.5) * mm, "end": v(-122, -15.87) * mm});
            skLineSegment(sketch, "E96.right", {"start": v(-124, 45.5) * mm, "end": v(-124, -15.87) * mm});
            skLineSegment(sketch, "E97.bottom", {"start": v(-126, 45.5) * mm, "end": v(-128, 45.5) * mm});
            skLineSegment(sketch, "E97.top", {"start": v(-126, -15.87) * mm, "end": v(-128, -15.87) * mm});
            skLineSegment(sketch, "E97.left", {"start": v(-126, 45.5) * mm, "end": v(-126, -15.87) * mm});
            skLineSegment(sketch, "E97.right", {"start": v(-128, 45.5) * mm, "end": v(-128, -15.87) * mm});
            skLineSegment(sketch, "E98.right", {"start": v(-130, 45.5) * mm, "end": v(-130, -15.87) * mm});
            skLineSegment(sketch, "E99.bottom", {"start": v(-132, 45.5) * mm, "end": v(-134, 45.5) * mm});
            skLineSegment(sketch, "E99.top", {"start": v(-132, -15.87) * mm, "end": v(-134, -15.87) * mm});
            skLineSegment(sketch, "E99.left", {"start": v(-132, 45.5) * mm, "end": v(-132, -15.87) * mm});
            skLineSegment(sketch, "E99.right", {"start": v(-134, 45.5) * mm, "end": v(-134, -15.87) * mm});
            skLineSegment(sketch, "E100.bottom", {"start": v(-136, 45.5) * mm, "end": v(-138, 45.5) * mm});
            skLineSegment(sketch, "E100.top", {"start": v(-136, -15.87) * mm, "end": v(-138, -15.87) * mm});
            skLineSegment(sketch, "E100.left", {"start": v(-136, 45.5) * mm, "end": v(-136, -15.87) * mm});
            skLineSegment(sketch, "E100.right", {"start": v(-138, 45.5) * mm, "end": v(-138, -15.87) * mm});
            skLineSegment(sketch, "E101.bottom", {"start": v(-140, 45.5) * mm, "end": v(-142, 45.5) * mm});
            skLineSegment(sketch, "E101.top", {"start": v(-140, -15.87) * mm, "end": v(-142, -15.87) * mm});
            skLineSegment(sketch, "E101.left", {"start": v(-140, 45.5) * mm, "end": v(-140, -15.87) * mm});
            skLineSegment(sketch, "E101.right", {"start": v(-142, 45.5) * mm, "end": v(-142, -15.87) * mm});
            skLineSegment(sketch, "E102.right", {"start": v(-144, 45.5) * mm, "end": v(-144, -15.87) * mm});
            skLineSegment(sketch, "E103.bottom", {"start": v(-146, 45.5) * mm, "end": v(-148, 45.5) * mm});
            skLineSegment(sketch, "E103.top", {"start": v(-146, -15.87) * mm, "end": v(-148, -15.87) * mm});
            skLineSegment(sketch, "E103.left", {"start": v(-146, 45.5) * mm, "end": v(-146, -15.87) * mm});
            skLineSegment(sketch, "E103.right", {"start": v(-148, 45.5) * mm, "end": v(-148, -15.87) * mm});
            skLineSegment(sketch, "E104.left", {"start": v(-150, 45.5) * mm, "end": v(-150, -15.87) * mm});
            skLineSegment(sketch, "E104.right", {"start": v(-152, 45.5) * mm, "end": v(-152, -15.87) * mm});
            skLineSegment(sketch, "E105.bottom", {"start": v(-154, 45.5) * mm, "end": v(-156, 45.5) * mm});
            skLineSegment(sketch, "E105.top", {"start": v(-154, -15.87) * mm, "end": v(-156, -15.87) * mm});
            skLineSegment(sketch, "E105.left", {"start": v(-154, 45.5) * mm, "end": v(-154, -15.87) * mm});
            skLineSegment(sketch, "E105.right", {"start": v(-156, 45.5) * mm, "end": v(-156, -15.87) * mm});
            skLineSegment(sketch, "E106.right", {"start": v(-158, 45.5) * mm, "end": v(-158, -15.87) * mm});
            skLineSegment(sketch, "E107.bottom", {"start": v(-160, 45.5) * mm, "end": v(-162, 45.5) * mm});
            skLineSegment(sketch, "E107.top", {"start": v(-160, -15.87) * mm, "end": v(-162, -15.87) * mm});
            skLineSegment(sketch, "E107.left", {"start": v(-160, 45.5) * mm, "end": v(-160, -15.87) * mm});
            skLineSegment(sketch, "E107.right", {"start": v(-162, 45.5) * mm, "end": v(-162, -15.87) * mm});
            skLineSegment(sketch, "E108.bottom", {"start": v(-164, 45.5) * mm, "end": v(-166, 45.5) * mm});
            skLineSegment(sketch, "E108.top", {"start": v(-164, -15.87) * mm, "end": v(-166, -15.87) * mm});
            skLineSegment(sketch, "E108.left", {"start": v(-164, 45.5) * mm, "end": v(-164, -15.87) * mm});
            skLineSegment(sketch, "E108.right", {"start": v(-166, 45.5) * mm, "end": v(-166, -15.87) * mm});
            skLineSegment(sketch, "E109.bottom", {"start": v(-168, 45.5) * mm, "end": v(-170, 45.5) * mm});
            skLineSegment(sketch, "E109.top", {"start": v(-168, -15.87) * mm, "end": v(-170, -15.87) * mm});
            skLineSegment(sketch, "E109.left", {"start": v(-168, 45.5) * mm, "end": v(-168, -15.87) * mm});
            skLineSegment(sketch, "E109.right", {"start": v(-170, 45.5) * mm, "end": v(-170, -15.87) * mm});
            skLineSegment(sketch, "E110.right", {"start": v(-172, 45.5) * mm, "end": v(-172, -15.87) * mm});
            skLineSegment(sketch, "E111.bottom", {"start": v(-174, 45.5) * mm, "end": v(-176, 45.5) * mm});
            skLineSegment(sketch, "E111.top", {"start": v(-174, -15.87) * mm, "end": v(-176, -15.87) * mm});
            skLineSegment(sketch, "E111.left", {"start": v(-174, 45.5) * mm, "end": v(-174, -15.87) * mm});
            skLineSegment(sketch, "E111.right", {"start": v(-176, 45.5) * mm, "end": v(-176, -15.87) * mm});
            skSolve(sketch);
        }
        {
            var Q0;
            {var subQ0=sQuery(id+"F13.wireOp",EDGE,"E61.right");Q0=makeQuery(id+"F13.imprint","IMPRINT",FACE,{"disambiguationData":[TD([[makeQuery(id+"F13.imprint","IMPRINT",EDGE,{"derivedFrom":subQ0}),-1.0]])]});}
            var Q1;
            {var subQ0=sQuery(id+"F13.wireOp",EDGE,"E62.right");Q1=makeQuery(id+"F13.imprint","IMPRINT",FACE,{"disambiguationData":[TD([[makeQuery(id+"F13.imprint","IMPRINT",EDGE,{"derivedFrom":subQ0}),-1.0]])]});}
            var Q2;
            Q2=makeQuery(id+"F13.imprint","IMPRINT",FACE,{"disambiguationData":[TD([[makeQuery(id+"F13.imprint","IMPRINT",EDGE,{"derivedFrom":sQuery(id+"F13.wireOp",EDGE,"E64.bottom")}),-1.0]])]});
            var Q3;
            Q3=makeQuery(id+"F13.imprint","IMPRINT",FACE,{"disambiguationData":[TD([[makeQuery(id+"F13.imprint","IMPRINT",EDGE,{"derivedFrom":sQuery(id+"F13.wireOp",EDGE,"E65.bottom")}),-1.0]])]});
            var Q4;
            Q4=makeQuery(id+"F13.imprint","IMPRINT",FACE,{"disambiguationData":[TD([[makeQuery(id+"F13.imprint","IMPRINT",EDGE,{"derivedFrom":sQuery(id+"F13.wireOp",EDGE,"E66.bottom")}),-1.0]])]});
            var Q5;
            {var subQ0=sQuery(id+"F13.wireOp",EDGE,"E67.right");Q5=makeQuery(id+"F13.imprint","IMPRINT",FACE,{"disambiguationData":[TD([[makeQuery(id+"F13.imprint","IMPRINT",EDGE,{"derivedFrom":subQ0}),-1.0]])]});}
            var Q6;
            {var subQ0=sQuery(id+"F13.wireOp",EDGE,"E68.right");Q6=makeQuery(id+"F13.imprint","IMPRINT",FACE,{"disambiguationData":[TD([[makeQuery(id+"F13.imprint","IMPRINT",EDGE,{"derivedFrom":subQ0}),-1.0]])]});}
            var Q7;
            {var subQ0=sQuery(id+"F13.wireOp",EDGE,"E69.right");Q7=makeQuery(id+"F13.imprint","IMPRINT",FACE,{"disambiguationData":[TD([[makeQuery(id+"F13.imprint","IMPRINT",EDGE,{"derivedFrom":subQ0}),-1.0]])]});}
            var Q8;
            {var subQ0=sQuery(id+"F13.wireOp",EDGE,"E70.right");Q8=makeQuery(id+"F13.imprint","IMPRINT",FACE,{"disambiguationData":[TD([[makeQuery(id+"F13.imprint","IMPRINT",EDGE,{"derivedFrom":subQ0}),-1.0]])]});}
            var Q9;
            Q9=makeQuery(id+"F13.imprint","IMPRINT",FACE,{"disambiguationData":[TD([[makeQuery(id+"F13.imprint","IMPRINT",EDGE,{"derivedFrom":sQuery(id+"F13.wireOp",EDGE,"E72.bottom")}),-1.0]])]});
            var Q10;
            Q10=makeQuery(id+"F13.imprint","IMPRINT",FACE,{"disambiguationData":[TD([[makeQuery(id+"F13.imprint","IMPRINT",EDGE,{"derivedFrom":sQuery(id+"F13.wireOp",EDGE,"E73.bottom")}),-1.0]])]});
            var Q11;
            Q11=makeQuery(id+"F13.imprint","IMPRINT",FACE,{"disambiguationData":[TD([[makeQuery(id+"F13.imprint","IMPRINT",EDGE,{"derivedFrom":sQuery(id+"F13.wireOp",EDGE,"E74.bottom")}),-1.0]])]});
            var Q12;
            {var subQ0=sQuery(id+"F13.wireOp",EDGE,"E75.right");Q12=makeQuery(id+"F13.imprint","IMPRINT",FACE,{"disambiguationData":[TD([[makeQuery(id+"F13.imprint","IMPRINT",EDGE,{"derivedFrom":subQ0}),-1.0]])]});}
            var Q13;
            {var subQ0=sQuery(id+"F13.wireOp",EDGE,"E76.right");Q13=makeQuery(id+"F13.imprint","IMPRINT",FACE,{"disambiguationData":[TD([[makeQuery(id+"F13.imprint","IMPRINT",EDGE,{"derivedFrom":subQ0}),-1.0]])]});}
            var Q14;
            {var subQ0=sQuery(id+"F13.wireOp",EDGE,"E77.right");Q14=makeQuery(id+"F13.imprint","IMPRINT",FACE,{"disambiguationData":[TD([[makeQuery(id+"F13.imprint","IMPRINT",EDGE,{"derivedFrom":subQ0}),-1.0]])]});}
            var Q15;
            {var subQ0=sQuery(id+"F13.wireOp",EDGE,"E78.right");Q15=makeQuery(id+"F13.imprint","IMPRINT",FACE,{"disambiguationData":[TD([[makeQuery(id+"F13.imprint","IMPRINT",EDGE,{"derivedFrom":subQ0}),-1.0]])]});}
            var Q16;
            Q16=makeQuery(id+"F13.imprint","IMPRINT",FACE,{"disambiguationData":[TD([[makeQuery(id+"F13.imprint","IMPRINT",EDGE,{"derivedFrom":sQuery(id+"F13.wireOp",EDGE,"E80.bottom")}),-1.0]])]});
            var Q17;
            Q17=makeQuery(id+"F13.imprint","IMPRINT",FACE,{"disambiguationData":[TD([[makeQuery(id+"F13.imprint","IMPRINT",EDGE,{"derivedFrom":sQuery(id+"F13.wireOp",EDGE,"E81.bottom")}),-1.0]])]});
            var Q18;
            Q18=makeQuery(id+"F13.imprint","IMPRINT",FACE,{"disambiguationData":[TD([[makeQuery(id+"F13.imprint","IMPRINT",EDGE,{"derivedFrom":sQuery(id+"F13.wireOp",EDGE,"E82.bottom")}),-1.0]])]});
            var Q19;
            {var subQ0=sQuery(id+"F13.wireOp",EDGE,"E83.right");Q19=makeQuery(id+"F13.imprint","IMPRINT",FACE,{"disambiguationData":[TD([[makeQuery(id+"F13.imprint","IMPRINT",EDGE,{"derivedFrom":subQ0}),-1.0]])]});}
            var Q20;
            {var subQ0=sQuery(id+"F13.wireOp",EDGE,"E84.right");Q20=makeQuery(id+"F13.imprint","IMPRINT",FACE,{"disambiguationData":[TD([[makeQuery(id+"F13.imprint","IMPRINT",EDGE,{"derivedFrom":subQ0}),-1.0]])]});}
            var Q21;
            {var subQ0=sQuery(id+"F13.wireOp",EDGE,"E85.right");Q21=makeQuery(id+"F13.imprint","IMPRINT",FACE,{"disambiguationData":[TD([[makeQuery(id+"F13.imprint","IMPRINT",EDGE,{"derivedFrom":subQ0}),-1.0]])]});}
            var Q22;
            {var subQ0=sQuery(id+"F13.wireOp",EDGE,"E86.right");Q22=makeQuery(id+"F13.imprint","IMPRINT",FACE,{"disambiguationData":[TD([[makeQuery(id+"F13.imprint","IMPRINT",EDGE,{"derivedFrom":subQ0}),-1.0]])]});}
            var Q23;
            Q23=makeQuery(id+"F13.imprint","IMPRINT",FACE,{"disambiguationData":[TD([[makeQuery(id+"F13.imprint","IMPRINT",EDGE,{"derivedFrom":sQuery(id+"F13.wireOp",EDGE,"E88.bottom")}),-1.0]])]});
            var Q24;
            Q24=makeQuery(id+"F13.imprint","IMPRINT",FACE,{"disambiguationData":[TD([[makeQuery(id+"F13.imprint","IMPRINT",EDGE,{"derivedFrom":sQuery(id+"F13.wireOp",EDGE,"E89.bottom")}),-1.0]])]});
            var Q25;
            Q25=makeQuery(id+"F13.imprint","IMPRINT",FACE,{"disambiguationData":[TD([[makeQuery(id+"F13.imprint","IMPRINT",EDGE,{"derivedFrom":sQuery(id+"F13.wireOp",EDGE,"E90.bottom")}),-1.0]])]});
            var Q26;
            {var subQ0=sQuery(id+"F13.wireOp",EDGE,"E91.right");Q26=makeQuery(id+"F13.imprint","IMPRINT",FACE,{"disambiguationData":[TD([[makeQuery(id+"F13.imprint","IMPRINT",EDGE,{"derivedFrom":subQ0}),-1.0]])]});}
            var Q27;
            {var subQ0=sQuery(id+"F13.wireOp",EDGE,"E92.right");Q27=makeQuery(id+"F13.imprint","IMPRINT",FACE,{"disambiguationData":[TD([[makeQuery(id+"F13.imprint","IMPRINT",EDGE,{"derivedFrom":subQ0}),-1.0]])]});}
            var Q28;
            {var subQ0=sQuery(id+"F13.wireOp",EDGE,"E93.right");Q28=makeQuery(id+"F13.imprint","IMPRINT",FACE,{"disambiguationData":[TD([[makeQuery(id+"F13.imprint","IMPRINT",EDGE,{"derivedFrom":subQ0}),-1.0]])]});}
            var Q29;
            Q29=makeQuery(id+"F13.imprint","IMPRINT",FACE,{"disambiguationData":[TD([[makeQuery(id+"F13.imprint","IMPRINT",EDGE,{"derivedFrom":sQuery(id+"F13.wireOp",EDGE,"E95.bottom")}),-1.0]])]});
            var Q30;
            Q30=makeQuery(id+"F13.imprint","IMPRINT",FACE,{"disambiguationData":[TD([[makeQuery(id+"F13.imprint","IMPRINT",EDGE,{"derivedFrom":sQuery(id+"F13.wireOp",EDGE,"E96.bottom")}),-1.0]])]});
            var Q31;
            Q31=makeQuery(id+"F13.imprint","IMPRINT",FACE,{"disambiguationData":[TD([[makeQuery(id+"F13.imprint","IMPRINT",EDGE,{"derivedFrom":sQuery(id+"F13.wireOp",EDGE,"E97.bottom")}),-1.0]])]});
            var Q32;
            {var subQ0=sQuery(id+"F13.wireOp",EDGE,"E98.right");Q32=makeQuery(id+"F13.imprint","IMPRINT",FACE,{"disambiguationData":[TD([[makeQuery(id+"F13.imprint","IMPRINT",EDGE,{"derivedFrom":subQ0}),-1.0]])]});}
            var Q33;
            {var subQ0=sQuery(id+"F13.wireOp",EDGE,"E99.right");Q33=makeQuery(id+"F13.imprint","IMPRINT",FACE,{"disambiguationData":[TD([[makeQuery(id+"F13.imprint","IMPRINT",EDGE,{"derivedFrom":subQ0}),-1.0]])]});}
            var Q34;
            {var subQ0=sQuery(id+"F13.wireOp",EDGE,"E100.right");Q34=makeQuery(id+"F13.imprint","IMPRINT",FACE,{"disambiguationData":[TD([[makeQuery(id+"F13.imprint","IMPRINT",EDGE,{"derivedFrom":subQ0}),-1.0]])]});}
            var Q35;
            {var subQ0=sQuery(id+"F13.wireOp",EDGE,"E101.right");Q35=makeQuery(id+"F13.imprint","IMPRINT",FACE,{"disambiguationData":[TD([[makeQuery(id+"F13.imprint","IMPRINT",EDGE,{"derivedFrom":subQ0}),-1.0]])]});}
            var Q36;
            Q36=makeQuery(id+"F13.imprint","IMPRINT",FACE,{"disambiguationData":[TD([[makeQuery(id+"F13.imprint","IMPRINT",EDGE,{"derivedFrom":sQuery(id+"F13.wireOp",EDGE,"E103.bottom")}),-1.0]])]});
            var Q37;
            {var subQ0=sQuery(id+"F13.wireOp",EDGE,"E104.left");Q37=makeQuery(id+"F13.imprint","IMPRINT",FACE,{"disambiguationData":[TD([[makeQuery(id+"F13.imprint","IMPRINT",EDGE,{"derivedFrom":subQ0}),-1.0]])]});}
            var Q38;
            Q38=makeQuery(id+"F13.imprint","IMPRINT",FACE,{"disambiguationData":[TD([[makeQuery(id+"F13.imprint","IMPRINT",EDGE,{"derivedFrom":sQuery(id+"F13.wireOp",EDGE,"E105.bottom")}),-1.0]])]});
            var Q39;
            {var subQ0=sQuery(id+"F13.wireOp",EDGE,"E106.right");Q39=makeQuery(id+"F13.imprint","IMPRINT",FACE,{"disambiguationData":[TD([[makeQuery(id+"F13.imprint","IMPRINT",EDGE,{"derivedFrom":subQ0}),-1.0]])]});}
            var Q40;
            {var subQ0=sQuery(id+"F13.wireOp",EDGE,"E107.right");Q40=makeQuery(id+"F13.imprint","IMPRINT",FACE,{"disambiguationData":[TD([[makeQuery(id+"F13.imprint","IMPRINT",EDGE,{"derivedFrom":subQ0}),-1.0]])]});}
            var Q41;
            {var subQ0=sQuery(id+"F13.wireOp",EDGE,"E108.right");Q41=makeQuery(id+"F13.imprint","IMPRINT",FACE,{"disambiguationData":[TD([[makeQuery(id+"F13.imprint","IMPRINT",EDGE,{"derivedFrom":subQ0}),-1.0]])]});}
            var Q42;
            {var subQ0=sQuery(id+"F13.wireOp",EDGE,"E109.right");Q42=makeQuery(id+"F13.imprint","IMPRINT",FACE,{"disambiguationData":[TD([[makeQuery(id+"F13.imprint","IMPRINT",EDGE,{"derivedFrom":subQ0}),-1.0]])]});}
            var Q43;
            Q43=makeQuery(id+"F13.imprint","IMPRINT",FACE,{"disambiguationData":[TD([[makeQuery(id+"F13.imprint","IMPRINT",EDGE,{"derivedFrom":sQuery(id+"F13.wireOp",EDGE,"E111.bottom")}),-1.0]])]});
            extrude(context, id + "F14", {"entities" : qUnion([Q0, Q1, Q2, Q3, Q4, Q5, Q6, Q7, Q8, Q9, Q10, Q11, Q12, Q13, Q14, Q15, Q16, Q17, Q18, Q19, Q20, Q21, Q22, Q23, Q24, Q25, Q26, Q27, Q28, Q29, Q30, Q31, Q32, Q33, Q34, Q35, Q36, Q37, Q38, Q39, Q40, Q41, Q42, Q43]), "operationType" : NewBodyOperationType.ADD, "depth" : 10 * mm, "offsetDistance" : 25 * mm});
        }
        {
            var Q0;
            Q0=makeQuery(id+"F3.opExtrude","SWEPT_FACE",FACE,{"disambiguationData":[OSD([sQuery(id+"F2.wireOp",EDGE,"E12")])]});
            var sketch = newSketch(context, id + "F15", { "sketchPlane" : qUnion([Q0])});
            skLineSegment(sketch, "E112.bottom", {"start": v(176, 45.23) * mm, "end": v(174, 45.23) * mm});
            skLineSegment(sketch, "E112.top", {"start": v(176, -16.14) * mm, "end": v(174, -16.14) * mm});
            skLineSegment(sketch, "E112.left", {"start": v(176, 45.23) * mm, "end": v(176, -16.14) * mm});
            skLineSegment(sketch, "E112.right", {"start": v(174, 45.23) * mm, "end": v(174, -16.14) * mm});
            skLineSegment(sketch, "E113.bottom", {"start": v(172, 45.23) * mm, "end": v(170, 45.23) * mm});
            skLineSegment(sketch, "E113.top", {"start": v(172, -16.14) * mm, "end": v(170, -16.14) * mm});
            skLineSegment(sketch, "E113.left", {"start": v(172, 45.23) * mm, "end": v(172, -16.14) * mm});
            skLineSegment(sketch, "E113.right", {"start": v(170, 45.23) * mm, "end": v(170, -16.14) * mm});
            skLineSegment(sketch, "E114.right", {"start": v(168, 45.23) * mm, "end": v(168, -16.14) * mm});
            skLineSegment(sketch, "E115.bottom", {"start": v(166, 45.23) * mm, "end": v(164, 45.23) * mm});
            skLineSegment(sketch, "E115.top", {"start": v(166, -16.14) * mm, "end": v(164, -16.14) * mm});
            skLineSegment(sketch, "E115.left", {"start": v(166, 45.23) * mm, "end": v(166, -16.14) * mm});
            skLineSegment(sketch, "E115.right", {"start": v(164, 45.23) * mm, "end": v(164, -16.14) * mm});
            skLineSegment(sketch, "E116.bottom", {"start": v(162, 45.23) * mm, "end": v(160, 45.23) * mm});
            skLineSegment(sketch, "E116.top", {"start": v(162, -16.14) * mm, "end": v(160, -16.14) * mm});
            skLineSegment(sketch, "E116.left", {"start": v(162, 45.23) * mm, "end": v(162, -16.14) * mm});
            skLineSegment(sketch, "E116.right", {"start": v(160, 45.23) * mm, "end": v(160, -16.14) * mm});
            skLineSegment(sketch, "E117.bottom", {"start": v(158, 45.23) * mm, "end": v(156, 45.23) * mm});
            skLineSegment(sketch, "E117.top", {"start": v(158, -16.14) * mm, "end": v(156, -16.14) * mm});
            skLineSegment(sketch, "E117.left", {"start": v(158, 45.23) * mm, "end": v(158, -16.14) * mm});
            skLineSegment(sketch, "E117.right", {"start": v(156, 45.23) * mm, "end": v(156, -16.14) * mm});
            skLineSegment(sketch, "E118.right", {"start": v(154, 45.23) * mm, "end": v(154, -16.14) * mm});
            skLineSegment(sketch, "E119.bottom", {"start": v(152, 45.23) * mm, "end": v(150, 45.23) * mm});
            skLineSegment(sketch, "E119.top", {"start": v(152, -16.14) * mm, "end": v(150, -16.14) * mm});
            skLineSegment(sketch, "E119.left", {"start": v(152, 45.23) * mm, "end": v(152, -16.14) * mm});
            skLineSegment(sketch, "E119.right", {"start": v(150, 45.23) * mm, "end": v(150, -16.14) * mm});
            skLineSegment(sketch, "E120.bottom", {"start": v(148, 45.23) * mm, "end": v(146, 45.23) * mm});
            skLineSegment(sketch, "E120.top", {"start": v(148, -16.14) * mm, "end": v(146, -16.14) * mm});
            skLineSegment(sketch, "E120.left", {"start": v(148, 45.23) * mm, "end": v(148, -16.14) * mm});
            skLineSegment(sketch, "E120.right", {"start": v(146, 45.23) * mm, "end": v(146, -16.14) * mm});
            skLineSegment(sketch, "E121.bottom", {"start": v(144, 45.23) * mm, "end": v(142, 45.23) * mm});
            skLineSegment(sketch, "E121.top", {"start": v(144, -16.14) * mm, "end": v(142, -16.14) * mm});
            skLineSegment(sketch, "E121.left", {"start": v(144, 45.23) * mm, "end": v(144, -16.14) * mm});
            skLineSegment(sketch, "E121.right", {"start": v(142, 45.23) * mm, "end": v(142, -16.14) * mm});
            skLineSegment(sketch, "E122.right", {"start": v(140, 45.23) * mm, "end": v(140, -16.14) * mm});
            skLineSegment(sketch, "E123.bottom", {"start": v(138, 45.23) * mm, "end": v(136, 45.23) * mm});
            skLineSegment(sketch, "E123.top", {"start": v(138, -16.14) * mm, "end": v(136, -16.14) * mm});
            skLineSegment(sketch, "E123.left", {"start": v(138, 45.23) * mm, "end": v(138, -16.14) * mm});
            skLineSegment(sketch, "E123.right", {"start": v(136, 45.23) * mm, "end": v(136, -16.14) * mm});
            skLineSegment(sketch, "E124.bottom", {"start": v(134, 45.23) * mm, "end": v(132, 45.23) * mm});
            skLineSegment(sketch, "E124.top", {"start": v(134, -16.14) * mm, "end": v(132, -16.14) * mm});
            skLineSegment(sketch, "E124.left", {"start": v(134, 45.23) * mm, "end": v(134, -16.14) * mm});
            skLineSegment(sketch, "E124.right", {"start": v(132, 45.23) * mm, "end": v(132, -16.14) * mm});
            skLineSegment(sketch, "E125.bottom", {"start": v(130, 45.23) * mm, "end": v(128, 45.23) * mm});
            skLineSegment(sketch, "E125.top", {"start": v(130, -16.14) * mm, "end": v(128, -16.14) * mm});
            skLineSegment(sketch, "E125.left", {"start": v(130, 45.23) * mm, "end": v(130, -16.14) * mm});
            skLineSegment(sketch, "E125.right", {"start": v(128, 45.23) * mm, "end": v(128, -16.14) * mm});
            skLineSegment(sketch, "E126.right", {"start": v(126, 45.23) * mm, "end": v(126, -16.14) * mm});
            skLineSegment(sketch, "E127.bottom", {"start": v(124, 45.23) * mm, "end": v(122, 45.23) * mm});
            skLineSegment(sketch, "E127.top", {"start": v(124, -16.14) * mm, "end": v(122, -16.14) * mm});
            skLineSegment(sketch, "E127.left", {"start": v(124, 45.23) * mm, "end": v(124, -16.14) * mm});
            skLineSegment(sketch, "E127.right", {"start": v(122, 45.23) * mm, "end": v(122, -16.14) * mm});
            skLineSegment(sketch, "E128.bottom", {"start": v(120, 45.23) * mm, "end": v(118, 45.23) * mm});
            skLineSegment(sketch, "E128.top", {"start": v(120, -16.14) * mm, "end": v(118, -16.14) * mm});
            skLineSegment(sketch, "E128.left", {"start": v(120, 45.23) * mm, "end": v(120, -16.14) * mm});
            skLineSegment(sketch, "E128.right", {"start": v(118, 45.23) * mm, "end": v(118, -16.14) * mm});
            skLineSegment(sketch, "E129.bottom", {"start": v(116, 45.23) * mm, "end": v(114, 45.23) * mm});
            skLineSegment(sketch, "E129.top", {"start": v(116, -16.14) * mm, "end": v(114, -16.14) * mm});
            skLineSegment(sketch, "E129.left", {"start": v(116, 45.23) * mm, "end": v(116, -16.14) * mm});
            skLineSegment(sketch, "E129.right", {"start": v(114, 45.23) * mm, "end": v(114, -16.14) * mm});
            skLineSegment(sketch, "E130.right", {"start": v(112, 45.23) * mm, "end": v(112, -16.14) * mm});
            skLineSegment(sketch, "E131.bottom", {"start": v(110, 45.23) * mm, "end": v(108, 45.23) * mm});
            skLineSegment(sketch, "E131.top", {"start": v(110, -16.14) * mm, "end": v(108, -16.14) * mm});
            skLineSegment(sketch, "E131.left", {"start": v(110, 45.23) * mm, "end": v(110, -16.14) * mm});
            skLineSegment(sketch, "E131.right", {"start": v(108, 45.23) * mm, "end": v(108, -16.14) * mm});
            skLineSegment(sketch, "E132.bottom", {"start": v(106, 45.23) * mm, "end": v(104, 45.23) * mm});
            skLineSegment(sketch, "E132.top", {"start": v(106, -16.14) * mm, "end": v(104, -16.14) * mm});
            skLineSegment(sketch, "E132.left", {"start": v(106, 45.23) * mm, "end": v(106, -16.14) * mm});
            skLineSegment(sketch, "E132.right", {"start": v(104, 45.23) * mm, "end": v(104, -16.14) * mm});
            skLineSegment(sketch, "E133.bottom", {"start": v(102, 45.23) * mm, "end": v(100, 45.23) * mm});
            skLineSegment(sketch, "E133.top", {"start": v(102, -16.14) * mm, "end": v(100, -16.14) * mm});
            skLineSegment(sketch, "E133.left", {"start": v(102, 45.23) * mm, "end": v(102, -16.14) * mm});
            skLineSegment(sketch, "E133.right", {"start": v(100, 45.23) * mm, "end": v(100, -16.14) * mm});
            skLineSegment(sketch, "E134.right", {"start": v(98, 45.23) * mm, "end": v(98, -16.14) * mm});
            skLineSegment(sketch, "E135.bottom", {"start": v(96, 45.23) * mm, "end": v(94, 45.23) * mm});
            skLineSegment(sketch, "E135.top", {"start": v(96, -16.14) * mm, "end": v(94, -16.14) * mm});
            skLineSegment(sketch, "E135.left", {"start": v(96, 45.23) * mm, "end": v(96, -16.14) * mm});
            skLineSegment(sketch, "E135.right", {"start": v(94, 45.23) * mm, "end": v(94, -16.14) * mm});
            skLineSegment(sketch, "E136.bottom", {"start": v(92, 45.23) * mm, "end": v(90, 45.23) * mm});
            skLineSegment(sketch, "E136.top", {"start": v(92, -16.14) * mm, "end": v(90, -16.14) * mm});
            skLineSegment(sketch, "E136.left", {"start": v(92, 45.23) * mm, "end": v(92, -16.14) * mm});
            skLineSegment(sketch, "E136.right", {"start": v(90, 45.23) * mm, "end": v(90, -16.14) * mm});
            skLineSegment(sketch, "E137.bottom", {"start": v(88, 45.23) * mm, "end": v(86, 45.23) * mm});
            skLineSegment(sketch, "E137.top", {"start": v(88, -16.14) * mm, "end": v(86, -16.14) * mm});
            skLineSegment(sketch, "E137.left", {"start": v(88, 45.23) * mm, "end": v(88, -16.14) * mm});
            skLineSegment(sketch, "E137.right", {"start": v(86, 45.23) * mm, "end": v(86, -16.14) * mm});
            skLineSegment(sketch, "E138.right", {"start": v(84, 45.23) * mm, "end": v(84, -16.14) * mm});
            skLineSegment(sketch, "E139.bottom", {"start": v(82, 45.23) * mm, "end": v(80, 45.23) * mm});
            skLineSegment(sketch, "E139.top", {"start": v(82, -16.14) * mm, "end": v(80, -16.14) * mm});
            skLineSegment(sketch, "E139.left", {"start": v(82, 45.23) * mm, "end": v(82, -16.14) * mm});
            skLineSegment(sketch, "E139.right", {"start": v(80, 45.23) * mm, "end": v(80, -16.14) * mm});
            skLineSegment(sketch, "E140.bottom", {"start": v(78, 45.23) * mm, "end": v(76, 45.23) * mm});
            skLineSegment(sketch, "E140.top", {"start": v(78, -16.14) * mm, "end": v(76, -16.14) * mm});
            skLineSegment(sketch, "E140.left", {"start": v(78, 45.23) * mm, "end": v(78, -16.14) * mm});
            skLineSegment(sketch, "E140.right", {"start": v(76, 45.23) * mm, "end": v(76, -16.14) * mm});
            skLineSegment(sketch, "E141.bottom", {"start": v(74, 45.23) * mm, "end": v(72, 45.23) * mm});
            skLineSegment(sketch, "E141.top", {"start": v(74, -16.14) * mm, "end": v(72, -16.14) * mm});
            skLineSegment(sketch, "E141.left", {"start": v(74, 45.23) * mm, "end": v(74, -16.14) * mm});
            skLineSegment(sketch, "E141.right", {"start": v(72, 45.23) * mm, "end": v(72, -16.14) * mm});
            skLineSegment(sketch, "E142.right", {"start": v(70, 45.23) * mm, "end": v(70, -16.14) * mm});
            skLineSegment(sketch, "E143.bottom", {"start": v(68, 45.23) * mm, "end": v(66, 45.23) * mm});
            skLineSegment(sketch, "E143.top", {"start": v(68, -16.14) * mm, "end": v(66, -16.14) * mm});
            skLineSegment(sketch, "E143.left", {"start": v(68, 45.23) * mm, "end": v(68, -16.14) * mm});
            skLineSegment(sketch, "E143.right", {"start": v(66, 45.23) * mm, "end": v(66, -16.14) * mm});
            skLineSegment(sketch, "E144.bottom", {"start": v(64, 45.23) * mm, "end": v(62, 45.23) * mm});
            skLineSegment(sketch, "E144.top", {"start": v(64, -16.14) * mm, "end": v(62, -16.14) * mm});
            skLineSegment(sketch, "E144.left", {"start": v(64, 45.23) * mm, "end": v(64, -16.14) * mm});
            skLineSegment(sketch, "E144.right", {"start": v(62, 45.23) * mm, "end": v(62, -16.14) * mm});
            skLineSegment(sketch, "E145.right", {"start": v(60, 45.23) * mm, "end": v(60, -16.14) * mm});
            skLineSegment(sketch, "E146.bottom", {"start": v(58, 45.23) * mm, "end": v(56, 45.23) * mm});
            skLineSegment(sketch, "E146.top", {"start": v(58, -16.14) * mm, "end": v(56, -16.14) * mm});
            skLineSegment(sketch, "E146.left", {"start": v(58, 45.23) * mm, "end": v(58, -16.14) * mm});
            skLineSegment(sketch, "E146.right", {"start": v(56, 45.23) * mm, "end": v(56, -16.14) * mm});
            skLineSegment(sketch, "E147.bottom", {"start": v(54, 45.23) * mm, "end": v(52, 45.23) * mm});
            skLineSegment(sketch, "E147.top", {"start": v(54, -16.14) * mm, "end": v(52, -16.14) * mm});
            skLineSegment(sketch, "E147.left", {"start": v(54, 45.23) * mm, "end": v(54, -16.14) * mm});
            skLineSegment(sketch, "E147.right", {"start": v(52, 45.23) * mm, "end": v(52, -16.14) * mm});
            skLineSegment(sketch, "E148.bottom", {"start": v(50, 45.23) * mm, "end": v(48, 45.23) * mm});
            skLineSegment(sketch, "E148.top", {"start": v(50, -16.14) * mm, "end": v(48, -16.14) * mm});
            skLineSegment(sketch, "E148.left", {"start": v(50, 45.23) * mm, "end": v(50, -16.14) * mm});
            skLineSegment(sketch, "E148.right", {"start": v(48, 45.23) * mm, "end": v(48, -16.14) * mm});
            skLineSegment(sketch, "E149.right", {"start": v(46, 45.23) * mm, "end": v(46, -16.14) * mm});
            skLineSegment(sketch, "E150.bottom", {"start": v(44, 45.23) * mm, "end": v(42, 45.23) * mm});
            skLineSegment(sketch, "E150.top", {"start": v(44, -16.14) * mm, "end": v(42, -16.14) * mm});
            skLineSegment(sketch, "E150.left", {"start": v(44, 45.23) * mm, "end": v(44, -16.14) * mm});
            skLineSegment(sketch, "E150.right", {"start": v(42, 45.23) * mm, "end": v(42, -16.14) * mm});
            skLineSegment(sketch, "E151.bottom", {"start": v(40, 45.23) * mm, "end": v(38, 45.23) * mm});
            skLineSegment(sketch, "E151.top", {"start": v(40, -16.14) * mm, "end": v(38, -16.14) * mm});
            skLineSegment(sketch, "E151.left", {"start": v(40, 45.23) * mm, "end": v(40, -16.14) * mm});
            skLineSegment(sketch, "E151.right", {"start": v(38, 45.23) * mm, "end": v(38, -16.14) * mm});
            skLineSegment(sketch, "E152.bottom", {"start": v(36, 45.23) * mm, "end": v(34, 45.23) * mm});
            skLineSegment(sketch, "E152.top", {"start": v(36, -16.14) * mm, "end": v(34, -16.14) * mm});
            skLineSegment(sketch, "E152.left", {"start": v(36, 45.23) * mm, "end": v(36, -16.14) * mm});
            skLineSegment(sketch, "E152.right", {"start": v(34, 45.23) * mm, "end": v(34, -16.14) * mm});
            skLineSegment(sketch, "E153.right", {"start": v(32, 45.23) * mm, "end": v(32, -16.14) * mm});
            skLineSegment(sketch, "E154.bottom", {"start": v(30, 45.23) * mm, "end": v(28, 45.23) * mm});
            skLineSegment(sketch, "E154.top", {"start": v(30, -16.14) * mm, "end": v(28, -16.14) * mm});
            skLineSegment(sketch, "E154.left", {"start": v(30, 45.23) * mm, "end": v(30, -16.14) * mm});
            skLineSegment(sketch, "E154.right", {"start": v(28, 45.23) * mm, "end": v(28, -16.14) * mm});
            skLineSegment(sketch, "E155.left", {"start": v(26, 45.23) * mm, "end": v(26, -16.14) * mm});
            skLineSegment(sketch, "E155.right", {"start": v(24, 45.23) * mm, "end": v(24, -16.14) * mm});
            skLineSegment(sketch, "E156.bottom", {"start": v(22, 45.23) * mm, "end": v(20, 45.23) * mm});
            skLineSegment(sketch, "E156.top", {"start": v(22, -16.14) * mm, "end": v(20, -16.14) * mm});
            skLineSegment(sketch, "E156.left", {"start": v(22, 45.23) * mm, "end": v(22, -16.14) * mm});
            skLineSegment(sketch, "E156.right", {"start": v(20, 45.23) * mm, "end": v(20, -16.14) * mm});
            skLineSegment(sketch, "E157.right", {"start": v(18, 45.23) * mm, "end": v(18, -16.14) * mm});
            skLineSegment(sketch, "E158.bottom", {"start": v(16, 45.23) * mm, "end": v(14, 45.23) * mm});
            skLineSegment(sketch, "E158.top", {"start": v(16, -16.14) * mm, "end": v(14, -16.14) * mm});
            skLineSegment(sketch, "E158.left", {"start": v(16, 45.23) * mm, "end": v(16, -16.14) * mm});
            skLineSegment(sketch, "E158.right", {"start": v(14, 45.23) * mm, "end": v(14, -16.14) * mm});
            skLineSegment(sketch, "E159.bottom", {"start": v(12, 45.23) * mm, "end": v(10, 45.23) * mm});
            skLineSegment(sketch, "E159.top", {"start": v(12, -16.14) * mm, "end": v(10, -16.14) * mm});
            skLineSegment(sketch, "E159.left", {"start": v(12, 45.23) * mm, "end": v(12, -16.14) * mm});
            skLineSegment(sketch, "E159.right", {"start": v(10, 45.23) * mm, "end": v(10, -16.14) * mm});
            skLineSegment(sketch, "E160.bottom", {"start": v(8, 45.23) * mm, "end": v(6, 45.23) * mm});
            skLineSegment(sketch, "E160.top", {"start": v(8, -16.14) * mm, "end": v(6, -16.14) * mm});
            skLineSegment(sketch, "E160.left", {"start": v(8, 45.23) * mm, "end": v(8, -16.14) * mm});
            skLineSegment(sketch, "E160.right", {"start": v(6, 45.23) * mm, "end": v(6, -16.14) * mm});
            skLineSegment(sketch, "E161.right", {"start": v(4, 45.23) * mm, "end": v(4, -16.14) * mm});
            skLineSegment(sketch, "E162.bottom", {"start": v(2, 45.23) * mm, "end": v(0, 45.23) * mm});
            skLineSegment(sketch, "E162.top", {"start": v(2, -16.14) * mm, "end": v(0, -16.14) * mm});
            skLineSegment(sketch, "E162.left", {"start": v(2, 45.23) * mm, "end": v(2, -16.14) * mm});
            skLineSegment(sketch, "E162.right", {"start": v(0, 45.23) * mm, "end": v(0, -16.14) * mm});
            skSolve(sketch);
        }
        {
            var Q0;
            {var subQ0=sQuery(id+"F15.wireOp",EDGE,"E162.top");Q0=makeQuery(id+"F15.imprint","IMPRINT",FACE,{"disambiguationData":[TD([[makeQuery(id+"F15.imprint","IMPRINT",EDGE,{"derivedFrom":subQ0}),-1.0]])]});}
            var Q1;
            {var subQ1=sQuery(id+"F2.wireOp",EDGE,"E12");var subQ2=makeQuery(id+"F3.opExtrude","SWEPT_EDGE",EDGE,{"disambiguationData":[OSD([subQ1,sQuery(id+"F2.wireOp",EDGE,"E25")])]});var subQ6=sQuery(id+"F15.wireOp",EDGE,"E161.right");var subQ8=makeQuery(id+"F15.imprint","INTERSECT",VERTEX,{"derivedFrom":[subQ2,subQ6]});Q1=makeQuery(id+"F15.imprint","IMPRINT",FACE,{"disambiguationData":[TD([[makeQuery(id+"F15.imprint","IMPRINT",EDGE,{"disambiguationData":[TD([[subQ8,1.0]])],"derivedFrom":subQ6}),1.0]])]});}
            var Q2;
            {var subQ0=sQuery(id+"F15.wireOp",EDGE,"E159.right");var subQ1=sQuery(id+"F2.wireOp",EDGE,"E12");var subQ4=makeQuery(id+"F3.opExtrude","SWEPT_EDGE",EDGE,{"disambiguationData":[OSD([subQ1,sQuery(id+"F2.wireOp",EDGE,"E29")])]});var subQ5=makeQuery(id+"F15.imprint","INTERSECT",VERTEX,{"derivedFrom":[subQ4,subQ0]});Q2=makeQuery(id+"F15.imprint","IMPRINT",FACE,{"disambiguationData":[TD([[makeQuery(id+"F15.imprint","IMPRINT",EDGE,{"disambiguationData":[TD([[subQ5,-1.0]])],"derivedFrom":subQ0}),-1.0]])]});}
            var Q3;
            {var subQ0=sQuery(id+"F15.wireOp",EDGE,"E158.right");var subQ1=sQuery(id+"F2.wireOp",EDGE,"E12");var subQ4=makeQuery(id+"F3.opExtrude","SWEPT_EDGE",EDGE,{"disambiguationData":[OSD([subQ1,sQuery(id+"F2.wireOp",EDGE,"E29")])]});var subQ5=makeQuery(id+"F15.imprint","INTERSECT",VERTEX,{"derivedFrom":[subQ4,subQ0]});Q3=makeQuery(id+"F15.imprint","IMPRINT",FACE,{"disambiguationData":[TD([[makeQuery(id+"F15.imprint","IMPRINT",EDGE,{"disambiguationData":[TD([[subQ5,-1.0]])],"derivedFrom":subQ0}),-1.0]])]});}
            var Q4;
            {var subQ0=sQuery(id+"F15.wireOp",EDGE,"E157.right");var subQ1=sQuery(id+"F2.wireOp",EDGE,"E12");var subQ2=makeQuery(id+"F3.opExtrude","SWEPT_EDGE",EDGE,{"disambiguationData":[OSD([subQ1,sQuery(id+"F2.wireOp",EDGE,"E25")])]});var subQ3=makeQuery(id+"F15.imprint","INTERSECT",VERTEX,{"derivedFrom":[subQ2,subQ0]});Q4=makeQuery(id+"F15.imprint","IMPRINT",FACE,{"disambiguationData":[TD([[makeQuery(id+"F15.imprint","IMPRINT",EDGE,{"disambiguationData":[TD([[subQ3,1.0]])],"derivedFrom":subQ0}),-1.0]])]});}
            var Q5;
            {var subQ0=sQuery(id+"F15.wireOp",EDGE,"E156.top");Q5=makeQuery(id+"F15.imprint","IMPRINT",FACE,{"disambiguationData":[TD([[makeQuery(id+"F15.imprint","IMPRINT",EDGE,{"derivedFrom":subQ0}),-1.0]])]});}
            var Q6;
            {var subQ0=sQuery(id+"F15.wireOp",EDGE,"E155.left");var subQ1=sQuery(id+"F2.wireOp",EDGE,"E12");var subQ2=makeQuery(id+"F3.opExtrude","SWEPT_EDGE",EDGE,{"disambiguationData":[OSD([subQ1,sQuery(id+"F2.wireOp",EDGE,"E25")])]});var subQ3=makeQuery(id+"F15.imprint","INTERSECT",VERTEX,{"derivedFrom":[subQ2,subQ0]});Q6=makeQuery(id+"F15.imprint","IMPRINT",FACE,{"disambiguationData":[TD([[makeQuery(id+"F15.imprint","IMPRINT",EDGE,{"disambiguationData":[TD([[subQ3,1.0]])],"derivedFrom":subQ0}),-1.0]])]});}
            var Q7;
            {var subQ0=sQuery(id+"F15.wireOp",EDGE,"E154.top");Q7=makeQuery(id+"F15.imprint","IMPRINT",FACE,{"disambiguationData":[TD([[makeQuery(id+"F15.imprint","IMPRINT",EDGE,{"derivedFrom":subQ0}),-1.0]])]});}
            var Q8;
            {var subQ1=sQuery(id+"F2.wireOp",EDGE,"E12");var subQ2=makeQuery(id+"F3.opExtrude","SWEPT_EDGE",EDGE,{"disambiguationData":[OSD([subQ1,sQuery(id+"F2.wireOp",EDGE,"E25")])]});var subQ6=sQuery(id+"F15.wireOp",EDGE,"E153.right");var subQ7=makeQuery(id+"F15.imprint","INTERSECT",VERTEX,{"derivedFrom":[subQ2,subQ6]});Q8=makeQuery(id+"F15.imprint","IMPRINT",FACE,{"disambiguationData":[TD([[makeQuery(id+"F15.imprint","IMPRINT",EDGE,{"disambiguationData":[TD([[subQ7,1.0]])],"derivedFrom":subQ6}),1.0]])]});}
            var Q9;
            {var subQ0=sQuery(id+"F15.wireOp",EDGE,"E151.right");var subQ1=sQuery(id+"F2.wireOp",EDGE,"E12");var subQ4=makeQuery(id+"F3.opExtrude","SWEPT_EDGE",EDGE,{"disambiguationData":[OSD([subQ1,sQuery(id+"F2.wireOp",EDGE,"E29")])]});var subQ5=makeQuery(id+"F15.imprint","INTERSECT",VERTEX,{"derivedFrom":[subQ4,subQ0]});Q9=makeQuery(id+"F15.imprint","IMPRINT",FACE,{"disambiguationData":[TD([[makeQuery(id+"F15.imprint","IMPRINT",EDGE,{"disambiguationData":[TD([[subQ5,-1.0]])],"derivedFrom":subQ0}),-1.0]])]});}
            var Q10;
            {var subQ0=sQuery(id+"F15.wireOp",EDGE,"E149.right");var subQ1=sQuery(id+"F2.wireOp",EDGE,"E12");var subQ2=makeQuery(id+"F3.opExtrude","SWEPT_EDGE",EDGE,{"disambiguationData":[OSD([subQ1,sQuery(id+"F2.wireOp",EDGE,"E25")])]});var subQ3=makeQuery(id+"F15.imprint","INTERSECT",VERTEX,{"derivedFrom":[subQ2,subQ0]});Q10=makeQuery(id+"F15.imprint","IMPRINT",FACE,{"disambiguationData":[TD([[makeQuery(id+"F15.imprint","IMPRINT",EDGE,{"disambiguationData":[TD([[subQ3,1.0]])],"derivedFrom":subQ0}),-1.0]])]});}
            var Q11;
            {var subQ0=sQuery(id+"F15.wireOp",EDGE,"E148.top");Q11=makeQuery(id+"F15.imprint","IMPRINT",FACE,{"disambiguationData":[TD([[makeQuery(id+"F15.imprint","IMPRINT",EDGE,{"derivedFrom":subQ0}),-1.0]])]});}
            var Q12;
            {var subQ0=sQuery(id+"F15.wireOp",EDGE,"E147.top");Q12=makeQuery(id+"F15.imprint","IMPRINT",FACE,{"disambiguationData":[TD([[makeQuery(id+"F15.imprint","IMPRINT",EDGE,{"derivedFrom":subQ0}),-1.0]])]});}
            var Q13;
            {var subQ0=sQuery(id+"F15.wireOp",EDGE,"E146.top");Q13=makeQuery(id+"F15.imprint","IMPRINT",FACE,{"disambiguationData":[TD([[makeQuery(id+"F15.imprint","IMPRINT",EDGE,{"derivedFrom":subQ0}),-1.0]])]});}
            var Q14;
            {var subQ0=sQuery(id+"F15.wireOp",EDGE,"E150.right");var subQ1=sQuery(id+"F2.wireOp",EDGE,"E12");var subQ4=makeQuery(id+"F3.opExtrude","SWEPT_EDGE",EDGE,{"disambiguationData":[OSD([subQ1,sQuery(id+"F2.wireOp",EDGE,"E29")])]});var subQ5=makeQuery(id+"F15.imprint","INTERSECT",VERTEX,{"derivedFrom":[subQ4,subQ0]});Q14=makeQuery(id+"F15.imprint","IMPRINT",FACE,{"disambiguationData":[TD([[makeQuery(id+"F15.imprint","IMPRINT",EDGE,{"disambiguationData":[TD([[subQ5,-1.0]])],"derivedFrom":subQ0}),-1.0]])]});}
            var Q15;
            {var subQ1=sQuery(id+"F2.wireOp",EDGE,"E12");var subQ2=makeQuery(id+"F3.opExtrude","SWEPT_EDGE",EDGE,{"disambiguationData":[OSD([subQ1,sQuery(id+"F2.wireOp",EDGE,"E25")])]});var subQ6=sQuery(id+"F15.wireOp",EDGE,"E145.right");var subQ7=makeQuery(id+"F15.imprint","INTERSECT",VERTEX,{"derivedFrom":[subQ2,subQ6]});Q15=makeQuery(id+"F15.imprint","IMPRINT",FACE,{"disambiguationData":[TD([[makeQuery(id+"F15.imprint","IMPRINT",EDGE,{"disambiguationData":[TD([[subQ7,1.0]])],"derivedFrom":subQ6}),1.0]])]});}
            var Q16;
            {var subQ0=sQuery(id+"F15.wireOp",EDGE,"E143.right");var subQ1=sQuery(id+"F2.wireOp",EDGE,"E12");var subQ4=makeQuery(id+"F3.opExtrude","SWEPT_EDGE",EDGE,{"disambiguationData":[OSD([subQ1,sQuery(id+"F2.wireOp",EDGE,"E29")])]});var subQ5=makeQuery(id+"F15.imprint","INTERSECT",VERTEX,{"derivedFrom":[subQ4,subQ0]});Q16=makeQuery(id+"F15.imprint","IMPRINT",FACE,{"disambiguationData":[TD([[makeQuery(id+"F15.imprint","IMPRINT",EDGE,{"disambiguationData":[TD([[subQ5,-1.0]])],"derivedFrom":subQ0}),-1.0]])]});}
            var Q17;
            {var subQ0=sQuery(id+"F15.wireOp",EDGE,"E142.right");var subQ1=sQuery(id+"F2.wireOp",EDGE,"E12");var subQ2=makeQuery(id+"F3.opExtrude","SWEPT_EDGE",EDGE,{"disambiguationData":[OSD([subQ1,sQuery(id+"F2.wireOp",EDGE,"E25")])]});var subQ3=makeQuery(id+"F15.imprint","INTERSECT",VERTEX,{"derivedFrom":[subQ2,subQ0]});Q17=makeQuery(id+"F15.imprint","IMPRINT",FACE,{"disambiguationData":[TD([[makeQuery(id+"F15.imprint","IMPRINT",EDGE,{"disambiguationData":[TD([[subQ3,1.0]])],"derivedFrom":subQ0}),-1.0]])]});}
            var Q18;
            {var subQ0=sQuery(id+"F15.wireOp",EDGE,"E141.top");Q18=makeQuery(id+"F15.imprint","IMPRINT",FACE,{"disambiguationData":[TD([[makeQuery(id+"F15.imprint","IMPRINT",EDGE,{"derivedFrom":subQ0}),-1.0]])]});}
            var Q19;
            {var subQ0=sQuery(id+"F15.wireOp",EDGE,"E140.top");Q19=makeQuery(id+"F15.imprint","IMPRINT",FACE,{"disambiguationData":[TD([[makeQuery(id+"F15.imprint","IMPRINT",EDGE,{"derivedFrom":subQ0}),-1.0]])]});}
            var Q20;
            {var subQ0=sQuery(id+"F15.wireOp",EDGE,"E139.top");Q20=makeQuery(id+"F15.imprint","IMPRINT",FACE,{"disambiguationData":[TD([[makeQuery(id+"F15.imprint","IMPRINT",EDGE,{"derivedFrom":subQ0}),-1.0]])]});}
            var Q21;
            {var subQ1=sQuery(id+"F2.wireOp",EDGE,"E12");var subQ2=makeQuery(id+"F3.opExtrude","SWEPT_EDGE",EDGE,{"disambiguationData":[OSD([subQ1,sQuery(id+"F2.wireOp",EDGE,"E25")])]});var subQ6=sQuery(id+"F15.wireOp",EDGE,"E138.right");var subQ7=makeQuery(id+"F15.imprint","INTERSECT",VERTEX,{"derivedFrom":[subQ2,subQ6]});Q21=makeQuery(id+"F15.imprint","IMPRINT",FACE,{"disambiguationData":[TD([[makeQuery(id+"F15.imprint","IMPRINT",EDGE,{"disambiguationData":[TD([[subQ7,1.0]])],"derivedFrom":subQ6}),1.0]])]});}
            var Q22;
            {var subQ0=sQuery(id+"F15.wireOp",EDGE,"E136.right");var subQ1=sQuery(id+"F2.wireOp",EDGE,"E12");var subQ4=makeQuery(id+"F3.opExtrude","SWEPT_EDGE",EDGE,{"disambiguationData":[OSD([subQ1,sQuery(id+"F2.wireOp",EDGE,"E29")])]});var subQ5=makeQuery(id+"F15.imprint","INTERSECT",VERTEX,{"derivedFrom":[subQ4,subQ0]});Q22=makeQuery(id+"F15.imprint","IMPRINT",FACE,{"disambiguationData":[TD([[makeQuery(id+"F15.imprint","IMPRINT",EDGE,{"disambiguationData":[TD([[subQ5,-1.0]])],"derivedFrom":subQ0}),-1.0]])]});}
            var Q23;
            {var subQ0=sQuery(id+"F15.wireOp",EDGE,"E135.right");var subQ1=sQuery(id+"F2.wireOp",EDGE,"E12");var subQ4=makeQuery(id+"F3.opExtrude","SWEPT_EDGE",EDGE,{"disambiguationData":[OSD([subQ1,sQuery(id+"F2.wireOp",EDGE,"E29")])]});var subQ5=makeQuery(id+"F15.imprint","INTERSECT",VERTEX,{"derivedFrom":[subQ4,subQ0]});Q23=makeQuery(id+"F15.imprint","IMPRINT",FACE,{"disambiguationData":[TD([[makeQuery(id+"F15.imprint","IMPRINT",EDGE,{"disambiguationData":[TD([[subQ5,-1.0]])],"derivedFrom":subQ0}),-1.0]])]});}
            var Q24;
            {var subQ0=sQuery(id+"F15.wireOp",EDGE,"E134.right");var subQ1=sQuery(id+"F2.wireOp",EDGE,"E12");var subQ2=makeQuery(id+"F3.opExtrude","SWEPT_EDGE",EDGE,{"disambiguationData":[OSD([subQ1,sQuery(id+"F2.wireOp",EDGE,"E25")])]});var subQ3=makeQuery(id+"F15.imprint","INTERSECT",VERTEX,{"derivedFrom":[subQ2,subQ0]});Q24=makeQuery(id+"F15.imprint","IMPRINT",FACE,{"disambiguationData":[TD([[makeQuery(id+"F15.imprint","IMPRINT",EDGE,{"disambiguationData":[TD([[subQ3,1.0]])],"derivedFrom":subQ0}),-1.0]])]});}
            var Q25;
            {var subQ0=sQuery(id+"F15.wireOp",EDGE,"E133.top");Q25=makeQuery(id+"F15.imprint","IMPRINT",FACE,{"disambiguationData":[TD([[makeQuery(id+"F15.imprint","IMPRINT",EDGE,{"derivedFrom":subQ0}),-1.0]])]});}
            var Q26;
            {var subQ0=sQuery(id+"F15.wireOp",EDGE,"E132.top");Q26=makeQuery(id+"F15.imprint","IMPRINT",FACE,{"disambiguationData":[TD([[makeQuery(id+"F15.imprint","IMPRINT",EDGE,{"derivedFrom":subQ0}),-1.0]])]});}
            var Q27;
            {var subQ0=sQuery(id+"F15.wireOp",EDGE,"E131.top");Q27=makeQuery(id+"F15.imprint","IMPRINT",FACE,{"disambiguationData":[TD([[makeQuery(id+"F15.imprint","IMPRINT",EDGE,{"derivedFrom":subQ0}),-1.0]])]});}
            var Q28;
            {var subQ1=sQuery(id+"F2.wireOp",EDGE,"E12");var subQ2=makeQuery(id+"F3.opExtrude","SWEPT_EDGE",EDGE,{"disambiguationData":[OSD([subQ1,sQuery(id+"F2.wireOp",EDGE,"E25")])]});var subQ6=sQuery(id+"F15.wireOp",EDGE,"E130.right");var subQ7=makeQuery(id+"F15.imprint","INTERSECT",VERTEX,{"derivedFrom":[subQ2,subQ6]});Q28=makeQuery(id+"F15.imprint","IMPRINT",FACE,{"disambiguationData":[TD([[makeQuery(id+"F15.imprint","IMPRINT",EDGE,{"disambiguationData":[TD([[subQ7,1.0]])],"derivedFrom":subQ6}),1.0]])]});}
            var Q29;
            {var subQ0=sQuery(id+"F15.wireOp",EDGE,"E128.right");var subQ1=sQuery(id+"F2.wireOp",EDGE,"E12");var subQ4=makeQuery(id+"F3.opExtrude","SWEPT_EDGE",EDGE,{"disambiguationData":[OSD([subQ1,sQuery(id+"F2.wireOp",EDGE,"E29")])]});var subQ5=makeQuery(id+"F15.imprint","INTERSECT",VERTEX,{"derivedFrom":[subQ4,subQ0]});Q29=makeQuery(id+"F15.imprint","IMPRINT",FACE,{"disambiguationData":[TD([[makeQuery(id+"F15.imprint","IMPRINT",EDGE,{"disambiguationData":[TD([[subQ5,-1.0]])],"derivedFrom":subQ0}),-1.0]])]});}
            var Q30;
            {var subQ0=sQuery(id+"F15.wireOp",EDGE,"E127.right");var subQ1=sQuery(id+"F2.wireOp",EDGE,"E12");var subQ4=makeQuery(id+"F3.opExtrude","SWEPT_EDGE",EDGE,{"disambiguationData":[OSD([subQ1,sQuery(id+"F2.wireOp",EDGE,"E29")])]});var subQ5=makeQuery(id+"F15.imprint","INTERSECT",VERTEX,{"derivedFrom":[subQ4,subQ0]});Q30=makeQuery(id+"F15.imprint","IMPRINT",FACE,{"disambiguationData":[TD([[makeQuery(id+"F15.imprint","IMPRINT",EDGE,{"disambiguationData":[TD([[subQ5,-1.0]])],"derivedFrom":subQ0}),-1.0]])]});}
            var Q31;
            {var subQ0=sQuery(id+"F15.wireOp",EDGE,"E126.right");var subQ1=sQuery(id+"F2.wireOp",EDGE,"E12");var subQ2=makeQuery(id+"F3.opExtrude","SWEPT_EDGE",EDGE,{"disambiguationData":[OSD([subQ1,sQuery(id+"F2.wireOp",EDGE,"E25")])]});var subQ3=makeQuery(id+"F15.imprint","INTERSECT",VERTEX,{"derivedFrom":[subQ2,subQ0]});Q31=makeQuery(id+"F15.imprint","IMPRINT",FACE,{"disambiguationData":[TD([[makeQuery(id+"F15.imprint","IMPRINT",EDGE,{"disambiguationData":[TD([[subQ3,1.0]])],"derivedFrom":subQ0}),-1.0]])]});}
            var Q32;
            {var subQ0=sQuery(id+"F15.wireOp",EDGE,"E125.top");Q32=makeQuery(id+"F15.imprint","IMPRINT",FACE,{"disambiguationData":[TD([[makeQuery(id+"F15.imprint","IMPRINT",EDGE,{"derivedFrom":subQ0}),-1.0]])]});}
            var Q33;
            {var subQ0=sQuery(id+"F15.wireOp",EDGE,"E124.top");Q33=makeQuery(id+"F15.imprint","IMPRINT",FACE,{"disambiguationData":[TD([[makeQuery(id+"F15.imprint","IMPRINT",EDGE,{"derivedFrom":subQ0}),-1.0]])]});}
            var Q34;
            {var subQ0=sQuery(id+"F15.wireOp",EDGE,"E123.top");Q34=makeQuery(id+"F15.imprint","IMPRINT",FACE,{"disambiguationData":[TD([[makeQuery(id+"F15.imprint","IMPRINT",EDGE,{"derivedFrom":subQ0}),-1.0]])]});}
            var Q35;
            {var subQ1=sQuery(id+"F2.wireOp",EDGE,"E12");var subQ2=makeQuery(id+"F3.opExtrude","SWEPT_EDGE",EDGE,{"disambiguationData":[OSD([subQ1,sQuery(id+"F2.wireOp",EDGE,"E25")])]});var subQ6=sQuery(id+"F15.wireOp",EDGE,"E122.right");var subQ7=makeQuery(id+"F15.imprint","INTERSECT",VERTEX,{"derivedFrom":[subQ2,subQ6]});Q35=makeQuery(id+"F15.imprint","IMPRINT",FACE,{"disambiguationData":[TD([[makeQuery(id+"F15.imprint","IMPRINT",EDGE,{"disambiguationData":[TD([[subQ7,1.0]])],"derivedFrom":subQ6}),1.0]])]});}
            var Q36;
            {var subQ0=sQuery(id+"F15.wireOp",EDGE,"E120.right");var subQ1=sQuery(id+"F2.wireOp",EDGE,"E12");var subQ4=makeQuery(id+"F3.opExtrude","SWEPT_EDGE",EDGE,{"disambiguationData":[OSD([subQ1,sQuery(id+"F2.wireOp",EDGE,"E29")])]});var subQ5=makeQuery(id+"F15.imprint","INTERSECT",VERTEX,{"derivedFrom":[subQ4,subQ0]});Q36=makeQuery(id+"F15.imprint","IMPRINT",FACE,{"disambiguationData":[TD([[makeQuery(id+"F15.imprint","IMPRINT",EDGE,{"disambiguationData":[TD([[subQ5,-1.0]])],"derivedFrom":subQ0}),-1.0]])]});}
            var Q37;
            {var subQ0=sQuery(id+"F15.wireOp",EDGE,"E119.right");var subQ1=sQuery(id+"F2.wireOp",EDGE,"E12");var subQ4=makeQuery(id+"F3.opExtrude","SWEPT_EDGE",EDGE,{"disambiguationData":[OSD([subQ1,sQuery(id+"F2.wireOp",EDGE,"E29")])]});var subQ5=makeQuery(id+"F15.imprint","INTERSECT",VERTEX,{"derivedFrom":[subQ4,subQ0]});Q37=makeQuery(id+"F15.imprint","IMPRINT",FACE,{"disambiguationData":[TD([[makeQuery(id+"F15.imprint","IMPRINT",EDGE,{"disambiguationData":[TD([[subQ5,-1.0]])],"derivedFrom":subQ0}),-1.0]])]});}
            var Q38;
            {var subQ0=sQuery(id+"F15.wireOp",EDGE,"E118.right");var subQ1=sQuery(id+"F2.wireOp",EDGE,"E12");var subQ2=makeQuery(id+"F3.opExtrude","SWEPT_EDGE",EDGE,{"disambiguationData":[OSD([subQ1,sQuery(id+"F2.wireOp",EDGE,"E25")])]});var subQ3=makeQuery(id+"F15.imprint","INTERSECT",VERTEX,{"derivedFrom":[subQ2,subQ0]});Q38=makeQuery(id+"F15.imprint","IMPRINT",FACE,{"disambiguationData":[TD([[makeQuery(id+"F15.imprint","IMPRINT",EDGE,{"disambiguationData":[TD([[subQ3,1.0]])],"derivedFrom":subQ0}),-1.0]])]});}
            var Q39;
            {var subQ0=sQuery(id+"F15.wireOp",EDGE,"E117.top");Q39=makeQuery(id+"F15.imprint","IMPRINT",FACE,{"disambiguationData":[TD([[makeQuery(id+"F15.imprint","IMPRINT",EDGE,{"derivedFrom":subQ0}),-1.0]])]});}
            var Q40;
            {var subQ0=sQuery(id+"F15.wireOp",EDGE,"E116.top");Q40=makeQuery(id+"F15.imprint","IMPRINT",FACE,{"disambiguationData":[TD([[makeQuery(id+"F15.imprint","IMPRINT",EDGE,{"derivedFrom":subQ0}),-1.0]])]});}
            var Q41;
            {var subQ0=sQuery(id+"F15.wireOp",EDGE,"E115.top");Q41=makeQuery(id+"F15.imprint","IMPRINT",FACE,{"disambiguationData":[TD([[makeQuery(id+"F15.imprint","IMPRINT",EDGE,{"derivedFrom":subQ0}),-1.0]])]});}
            var Q42;
            {var subQ1=sQuery(id+"F2.wireOp",EDGE,"E12");var subQ2=makeQuery(id+"F3.opExtrude","SWEPT_EDGE",EDGE,{"disambiguationData":[OSD([subQ1,sQuery(id+"F2.wireOp",EDGE,"E25")])]});var subQ6=sQuery(id+"F15.wireOp",EDGE,"E114.right");var subQ7=makeQuery(id+"F15.imprint","INTERSECT",VERTEX,{"derivedFrom":[subQ2,subQ6]});Q42=makeQuery(id+"F15.imprint","IMPRINT",FACE,{"disambiguationData":[TD([[makeQuery(id+"F15.imprint","IMPRINT",EDGE,{"disambiguationData":[TD([[subQ7,1.0]])],"derivedFrom":subQ6}),1.0]])]});}
            var Q43;
            {var subQ0=sQuery(id+"F15.wireOp",EDGE,"E112.right");var subQ1=sQuery(id+"F2.wireOp",EDGE,"E12");var subQ4=makeQuery(id+"F3.opExtrude","SWEPT_EDGE",EDGE,{"disambiguationData":[OSD([subQ1,sQuery(id+"F2.wireOp",EDGE,"E29")])]});var subQ5=makeQuery(id+"F15.imprint","INTERSECT",VERTEX,{"derivedFrom":[subQ4,subQ0]});Q43=makeQuery(id+"F15.imprint","IMPRINT",FACE,{"disambiguationData":[TD([[makeQuery(id+"F15.imprint","IMPRINT",EDGE,{"disambiguationData":[TD([[subQ5,-1.0]])],"derivedFrom":subQ0}),-1.0]])]});}
            extrude(context, id + "F16", {"entities" : qUnion([Q0, Q1, Q2, Q3, Q4, Q5, Q6, Q7, Q8, Q9, Q10, Q11, Q12, Q13, Q14, Q15, Q16, Q17, Q18, Q19, Q20, Q21, Q22, Q23, Q24, Q25, Q26, Q27, Q28, Q29, Q30, Q31, Q32, Q33, Q34, Q35, Q36, Q37, Q38, Q39, Q40, Q41, Q42, Q43]), "operationType" : NewBodyOperationType.ADD, "depth" : 10 * mm, "offsetDistance" : 25 * mm});
        }
        {
            var Q0;
            {var subQ0=sQuery(id+"F2.wireOp",EDGE,"E34");var subQ1=sQuery(id+"F2.wireOp",EDGE,"E21");var subQ2=makeQuery(id+"F3.opExtrude","SWEPT_EDGE",EDGE,{"disambiguationData":[OSD([subQ1,subQ0])]});Q0=makeQuery(id+"F14.opExtrude","CAP_EDGE",EDGE,{"disambiguationData":[OSD([subQ1,subQ0]),TDD([makeQuery(id+"F13.imprint","IMPRINT",EDGE,{"disambiguationData":[TD([[makeQuery(id+"F13.imprint","INTERSECT",VERTEX,{"derivedFrom":[subQ2,sQuery(id+"F13.wireOp",EDGE,"E61.bottom"),sQuery(id+"F13.wireOp",EDGE,"E61.right")]}),1.0]])],"derivedFrom":subQ2})])],"isStart":false});}
            var Q1;
            {var subQ0=sQuery(id+"F2.wireOp",EDGE,"E34");var subQ1=sQuery(id+"F2.wireOp",EDGE,"E21");var subQ2=makeQuery(id+"F3.opExtrude","SWEPT_EDGE",EDGE,{"disambiguationData":[OSD([subQ1,subQ0])]});Q1=makeQuery(id+"F14.opExtrude","CAP_EDGE",EDGE,{"disambiguationData":[OSD([subQ1,subQ0]),TDD([makeQuery(id+"F13.imprint","IMPRINT",EDGE,{"disambiguationData":[TD([[makeQuery(id+"F13.imprint","INTERSECT",VERTEX,{"derivedFrom":[subQ2,sQuery(id+"F13.wireOp",EDGE,"E63.right")]}),-1.0]])],"derivedFrom":subQ2})])],"isStart":false});}
            var Q2;
            Q2=makeQuery(id+"F14.opExtrude","CAP_EDGE",EDGE,{"disambiguationData":[OSD([sQuery(id+"F13.wireOp",EDGE,"E64.bottom")])],"isStart":false});
            var Q3;
            Q3=makeQuery(id+"F14.opExtrude","CAP_EDGE",EDGE,{"disambiguationData":[OSD([sQuery(id+"F13.wireOp",EDGE,"E65.bottom")])],"isStart":false});
            var Q4;
            Q4=makeQuery(id+"F14.opExtrude","CAP_EDGE",EDGE,{"disambiguationData":[OSD([sQuery(id+"F13.wireOp",EDGE,"E66.bottom")])],"isStart":false});
            var Q5;
            {var subQ0=sQuery(id+"F2.wireOp",EDGE,"E34");var subQ1=sQuery(id+"F2.wireOp",EDGE,"E21");var subQ2=makeQuery(id+"F3.opExtrude","SWEPT_EDGE",EDGE,{"disambiguationData":[OSD([subQ1,subQ0])]});Q5=makeQuery(id+"F14.opExtrude","CAP_EDGE",EDGE,{"disambiguationData":[OSD([subQ1,subQ0]),TDD([makeQuery(id+"F13.imprint","IMPRINT",EDGE,{"disambiguationData":[TD([[makeQuery(id+"F13.imprint","INTERSECT",VERTEX,{"derivedFrom":[subQ2,sQuery(id+"F13.wireOp",EDGE,"E67.right")]}),1.0]])],"derivedFrom":subQ2})])],"isStart":false});}
            var Q6;
            {var subQ0=sQuery(id+"F2.wireOp",EDGE,"E34");var subQ1=sQuery(id+"F2.wireOp",EDGE,"E21");var subQ2=makeQuery(id+"F3.opExtrude","SWEPT_EDGE",EDGE,{"disambiguationData":[OSD([subQ1,subQ0])]});Q6=makeQuery(id+"F14.opExtrude","CAP_EDGE",EDGE,{"disambiguationData":[OSD([subQ1,subQ0]),TDD([makeQuery(id+"F13.imprint","IMPRINT",EDGE,{"disambiguationData":[TD([[makeQuery(id+"F13.imprint","INTERSECT",VERTEX,{"derivedFrom":[subQ2,sQuery(id+"F13.wireOp",EDGE,"E68.bottom"),sQuery(id+"F13.wireOp",EDGE,"E68.right")]}),1.0]])],"derivedFrom":subQ2})])],"isStart":false});}
            var Q7;
            {var subQ0=sQuery(id+"F2.wireOp",EDGE,"E34");var subQ1=sQuery(id+"F2.wireOp",EDGE,"E21");var subQ2=makeQuery(id+"F3.opExtrude","SWEPT_EDGE",EDGE,{"disambiguationData":[OSD([subQ1,subQ0])]});Q7=makeQuery(id+"F14.opExtrude","CAP_EDGE",EDGE,{"disambiguationData":[OSD([subQ1,subQ0]),TDD([makeQuery(id+"F13.imprint","IMPRINT",EDGE,{"disambiguationData":[TD([[makeQuery(id+"F13.imprint","INTERSECT",VERTEX,{"derivedFrom":[subQ2,sQuery(id+"F13.wireOp",EDGE,"E69.bottom"),sQuery(id+"F13.wireOp",EDGE,"E69.right")]}),1.0]])],"derivedFrom":subQ2})])],"isStart":false});}
            var Q8;
            {var subQ0=sQuery(id+"F2.wireOp",EDGE,"E34");var subQ1=sQuery(id+"F2.wireOp",EDGE,"E21");var subQ2=makeQuery(id+"F3.opExtrude","SWEPT_EDGE",EDGE,{"disambiguationData":[OSD([subQ1,subQ0])]});Q8=makeQuery(id+"F14.opExtrude","CAP_EDGE",EDGE,{"disambiguationData":[OSD([subQ1,subQ0]),TDD([makeQuery(id+"F13.imprint","IMPRINT",EDGE,{"disambiguationData":[TD([[makeQuery(id+"F13.imprint","INTERSECT",VERTEX,{"derivedFrom":[subQ2,sQuery(id+"F13.wireOp",EDGE,"E71.right")]}),-1.0]])],"derivedFrom":subQ2})])],"isStart":false});}
            var Q9;
            Q9=makeQuery(id+"F14.opExtrude","CAP_EDGE",EDGE,{"disambiguationData":[OSD([sQuery(id+"F13.wireOp",EDGE,"E72.bottom")])],"isStart":false});
            var Q10;
            Q10=makeQuery(id+"F14.opExtrude","CAP_EDGE",EDGE,{"disambiguationData":[OSD([sQuery(id+"F13.wireOp",EDGE,"E73.bottom")])],"isStart":false});
            var Q11;
            Q11=makeQuery(id+"F14.opExtrude","CAP_EDGE",EDGE,{"disambiguationData":[OSD([sQuery(id+"F13.wireOp",EDGE,"E74.bottom")])],"isStart":false});
            var Q12;
            {var subQ0=sQuery(id+"F2.wireOp",EDGE,"E34");var subQ1=sQuery(id+"F2.wireOp",EDGE,"E21");var subQ2=makeQuery(id+"F3.opExtrude","SWEPT_EDGE",EDGE,{"disambiguationData":[OSD([subQ1,subQ0])]});Q12=makeQuery(id+"F14.opExtrude","CAP_EDGE",EDGE,{"disambiguationData":[OSD([subQ1,subQ0]),TDD([makeQuery(id+"F13.imprint","IMPRINT",EDGE,{"disambiguationData":[TD([[makeQuery(id+"F13.imprint","INTERSECT",VERTEX,{"derivedFrom":[subQ2,sQuery(id+"F13.wireOp",EDGE,"E75.right")]}),1.0]])],"derivedFrom":subQ2})])],"isStart":false});}
            var Q13;
            {var subQ0=sQuery(id+"F2.wireOp",EDGE,"E34");var subQ1=sQuery(id+"F2.wireOp",EDGE,"E21");var subQ2=makeQuery(id+"F3.opExtrude","SWEPT_EDGE",EDGE,{"disambiguationData":[OSD([subQ1,subQ0])]});Q13=makeQuery(id+"F14.opExtrude","CAP_EDGE",EDGE,{"disambiguationData":[OSD([subQ1,subQ0]),TDD([makeQuery(id+"F13.imprint","IMPRINT",EDGE,{"disambiguationData":[TD([[makeQuery(id+"F13.imprint","INTERSECT",VERTEX,{"derivedFrom":[subQ2,sQuery(id+"F13.wireOp",EDGE,"E76.bottom"),sQuery(id+"F13.wireOp",EDGE,"E76.right")]}),1.0]])],"derivedFrom":subQ2})])],"isStart":false});}
            var Q14;
            {var subQ0=sQuery(id+"F2.wireOp",EDGE,"E34");var subQ1=sQuery(id+"F2.wireOp",EDGE,"E21");var subQ2=makeQuery(id+"F3.opExtrude","SWEPT_EDGE",EDGE,{"disambiguationData":[OSD([subQ1,subQ0])]});Q14=makeQuery(id+"F14.opExtrude","CAP_EDGE",EDGE,{"disambiguationData":[OSD([subQ1,subQ0]),TDD([makeQuery(id+"F13.imprint","IMPRINT",EDGE,{"disambiguationData":[TD([[makeQuery(id+"F13.imprint","INTERSECT",VERTEX,{"derivedFrom":[subQ2,sQuery(id+"F13.wireOp",EDGE,"E77.bottom"),sQuery(id+"F13.wireOp",EDGE,"E77.right")]}),1.0]])],"derivedFrom":subQ2})])],"isStart":false});}
            var Q15;
            {var subQ0=sQuery(id+"F2.wireOp",EDGE,"E34");var subQ1=sQuery(id+"F2.wireOp",EDGE,"E21");var subQ2=makeQuery(id+"F3.opExtrude","SWEPT_EDGE",EDGE,{"disambiguationData":[OSD([subQ1,subQ0])]});Q15=makeQuery(id+"F14.opExtrude","CAP_EDGE",EDGE,{"disambiguationData":[OSD([subQ1,subQ0]),TDD([makeQuery(id+"F13.imprint","IMPRINT",EDGE,{"disambiguationData":[TD([[makeQuery(id+"F13.imprint","INTERSECT",VERTEX,{"derivedFrom":[subQ2,sQuery(id+"F13.wireOp",EDGE,"E79.right")]}),-1.0]])],"derivedFrom":subQ2})])],"isStart":false});}
            var Q16;
            Q16=makeQuery(id+"F14.opExtrude","CAP_EDGE",EDGE,{"disambiguationData":[OSD([sQuery(id+"F13.wireOp",EDGE,"E80.bottom")])],"isStart":false});
            var Q17;
            Q17=makeQuery(id+"F14.opExtrude","CAP_EDGE",EDGE,{"disambiguationData":[OSD([sQuery(id+"F13.wireOp",EDGE,"E81.bottom")])],"isStart":false});
            var Q18;
            Q18=makeQuery(id+"F14.opExtrude","CAP_EDGE",EDGE,{"disambiguationData":[OSD([sQuery(id+"F13.wireOp",EDGE,"E82.bottom")])],"isStart":false});
            var Q19;
            {var subQ0=sQuery(id+"F2.wireOp",EDGE,"E34");var subQ1=sQuery(id+"F2.wireOp",EDGE,"E21");var subQ2=makeQuery(id+"F3.opExtrude","SWEPT_EDGE",EDGE,{"disambiguationData":[OSD([subQ1,subQ0])]});Q19=makeQuery(id+"F14.opExtrude","CAP_EDGE",EDGE,{"disambiguationData":[OSD([subQ1,subQ0]),TDD([makeQuery(id+"F13.imprint","IMPRINT",EDGE,{"disambiguationData":[TD([[makeQuery(id+"F13.imprint","INTERSECT",VERTEX,{"derivedFrom":[subQ2,sQuery(id+"F13.wireOp",EDGE,"E83.right")]}),1.0]])],"derivedFrom":subQ2})])],"isStart":false});}
            var Q20;
            {var subQ0=sQuery(id+"F2.wireOp",EDGE,"E34");var subQ1=sQuery(id+"F2.wireOp",EDGE,"E21");var subQ2=makeQuery(id+"F3.opExtrude","SWEPT_EDGE",EDGE,{"disambiguationData":[OSD([subQ1,subQ0])]});Q20=makeQuery(id+"F14.opExtrude","CAP_EDGE",EDGE,{"disambiguationData":[OSD([subQ1,subQ0]),TDD([makeQuery(id+"F13.imprint","IMPRINT",EDGE,{"disambiguationData":[TD([[makeQuery(id+"F13.imprint","INTERSECT",VERTEX,{"derivedFrom":[subQ2,sQuery(id+"F13.wireOp",EDGE,"E84.bottom"),sQuery(id+"F13.wireOp",EDGE,"E84.right")]}),1.0]])],"derivedFrom":subQ2})])],"isStart":false});}
            var Q21;
            {var subQ0=sQuery(id+"F2.wireOp",EDGE,"E34");var subQ1=sQuery(id+"F2.wireOp",EDGE,"E21");var subQ2=makeQuery(id+"F3.opExtrude","SWEPT_EDGE",EDGE,{"disambiguationData":[OSD([subQ1,subQ0])]});Q21=makeQuery(id+"F14.opExtrude","CAP_EDGE",EDGE,{"disambiguationData":[OSD([subQ1,subQ0]),TDD([makeQuery(id+"F13.imprint","IMPRINT",EDGE,{"disambiguationData":[TD([[makeQuery(id+"F13.imprint","INTERSECT",VERTEX,{"derivedFrom":[subQ2,sQuery(id+"F13.wireOp",EDGE,"E85.bottom"),sQuery(id+"F13.wireOp",EDGE,"E85.right")]}),1.0]])],"derivedFrom":subQ2})])],"isStart":false});}
            var Q22;
            {var subQ0=sQuery(id+"F2.wireOp",EDGE,"E34");var subQ1=sQuery(id+"F2.wireOp",EDGE,"E21");var subQ2=makeQuery(id+"F3.opExtrude","SWEPT_EDGE",EDGE,{"disambiguationData":[OSD([subQ1,subQ0])]});Q22=makeQuery(id+"F14.opExtrude","CAP_EDGE",EDGE,{"disambiguationData":[OSD([subQ1,subQ0]),TDD([makeQuery(id+"F13.imprint","IMPRINT",EDGE,{"disambiguationData":[TD([[makeQuery(id+"F13.imprint","INTERSECT",VERTEX,{"derivedFrom":[subQ2,sQuery(id+"F13.wireOp",EDGE,"E87.right")]}),-1.0]])],"derivedFrom":subQ2})])],"isStart":false});}
            var Q23;
            Q23=makeQuery(id+"F14.opExtrude","CAP_EDGE",EDGE,{"disambiguationData":[OSD([sQuery(id+"F13.wireOp",EDGE,"E88.bottom")])],"isStart":false});
            var Q24;
            Q24=makeQuery(id+"F14.opExtrude","CAP_EDGE",EDGE,{"disambiguationData":[OSD([sQuery(id+"F13.wireOp",EDGE,"E89.bottom")])],"isStart":false});
            var Q25;
            Q25=makeQuery(id+"F14.opExtrude","CAP_EDGE",EDGE,{"disambiguationData":[OSD([sQuery(id+"F13.wireOp",EDGE,"E90.bottom")])],"isStart":false});
            var Q26;
            {var subQ0=sQuery(id+"F2.wireOp",EDGE,"E34");var subQ1=sQuery(id+"F2.wireOp",EDGE,"E21");var subQ2=makeQuery(id+"F3.opExtrude","SWEPT_EDGE",EDGE,{"disambiguationData":[OSD([subQ1,subQ0])]});Q26=makeQuery(id+"F14.opExtrude","CAP_EDGE",EDGE,{"disambiguationData":[OSD([subQ1,subQ0]),TDD([makeQuery(id+"F13.imprint","IMPRINT",EDGE,{"disambiguationData":[TD([[makeQuery(id+"F13.imprint","INTERSECT",VERTEX,{"derivedFrom":[subQ2,sQuery(id+"F13.wireOp",EDGE,"E91.right")]}),1.0]])],"derivedFrom":subQ2})])],"isStart":false});}
            var Q27;
            {var subQ0=sQuery(id+"F2.wireOp",EDGE,"E34");var subQ1=sQuery(id+"F2.wireOp",EDGE,"E21");var subQ2=makeQuery(id+"F3.opExtrude","SWEPT_EDGE",EDGE,{"disambiguationData":[OSD([subQ1,subQ0])]});Q27=makeQuery(id+"F14.opExtrude","CAP_EDGE",EDGE,{"disambiguationData":[OSD([subQ1,subQ0]),TDD([makeQuery(id+"F13.imprint","IMPRINT",EDGE,{"disambiguationData":[TD([[makeQuery(id+"F13.imprint","INTERSECT",VERTEX,{"derivedFrom":[subQ2,sQuery(id+"F13.wireOp",EDGE,"E92.bottom"),sQuery(id+"F13.wireOp",EDGE,"E92.right")]}),1.0]])],"derivedFrom":subQ2})])],"isStart":false});}
            var Q28;
            {var subQ0=sQuery(id+"F2.wireOp",EDGE,"E34");var subQ1=sQuery(id+"F2.wireOp",EDGE,"E21");var subQ2=makeQuery(id+"F3.opExtrude","SWEPT_EDGE",EDGE,{"disambiguationData":[OSD([subQ1,subQ0])]});Q28=makeQuery(id+"F14.opExtrude","CAP_EDGE",EDGE,{"disambiguationData":[OSD([subQ1,subQ0]),TDD([makeQuery(id+"F13.imprint","IMPRINT",EDGE,{"disambiguationData":[TD([[makeQuery(id+"F13.imprint","INTERSECT",VERTEX,{"derivedFrom":[subQ2,sQuery(id+"F13.wireOp",EDGE,"E94.right")]}),-1.0]])],"derivedFrom":subQ2})])],"isStart":false});}
            var Q29;
            Q29=makeQuery(id+"F14.opExtrude","CAP_EDGE",EDGE,{"disambiguationData":[OSD([sQuery(id+"F13.wireOp",EDGE,"E95.bottom")])],"isStart":false});
            var Q30;
            Q30=makeQuery(id+"F14.opExtrude","CAP_EDGE",EDGE,{"disambiguationData":[OSD([sQuery(id+"F13.wireOp",EDGE,"E96.bottom")])],"isStart":false});
            var Q31;
            Q31=makeQuery(id+"F14.opExtrude","CAP_EDGE",EDGE,{"disambiguationData":[OSD([sQuery(id+"F13.wireOp",EDGE,"E97.bottom")])],"isStart":false});
            var Q32;
            {var subQ0=sQuery(id+"F2.wireOp",EDGE,"E34");var subQ1=sQuery(id+"F2.wireOp",EDGE,"E21");var subQ2=makeQuery(id+"F3.opExtrude","SWEPT_EDGE",EDGE,{"disambiguationData":[OSD([subQ1,subQ0])]});Q32=makeQuery(id+"F14.opExtrude","CAP_EDGE",EDGE,{"disambiguationData":[OSD([subQ1,subQ0]),TDD([makeQuery(id+"F13.imprint","IMPRINT",EDGE,{"disambiguationData":[TD([[makeQuery(id+"F13.imprint","INTERSECT",VERTEX,{"derivedFrom":[subQ2,sQuery(id+"F13.wireOp",EDGE,"E98.right")]}),1.0]])],"derivedFrom":subQ2})])],"isStart":false});}
            var Q33;
            {var subQ0=sQuery(id+"F2.wireOp",EDGE,"E34");var subQ1=sQuery(id+"F2.wireOp",EDGE,"E21");var subQ2=makeQuery(id+"F3.opExtrude","SWEPT_EDGE",EDGE,{"disambiguationData":[OSD([subQ1,subQ0])]});Q33=makeQuery(id+"F14.opExtrude","CAP_EDGE",EDGE,{"disambiguationData":[OSD([subQ1,subQ0]),TDD([makeQuery(id+"F13.imprint","IMPRINT",EDGE,{"disambiguationData":[TD([[makeQuery(id+"F13.imprint","INTERSECT",VERTEX,{"derivedFrom":[subQ2,sQuery(id+"F13.wireOp",EDGE,"E99.bottom"),sQuery(id+"F13.wireOp",EDGE,"E99.right")]}),1.0]])],"derivedFrom":subQ2})])],"isStart":false});}
            var Q34;
            {var subQ0=sQuery(id+"F2.wireOp",EDGE,"E34");var subQ1=sQuery(id+"F2.wireOp",EDGE,"E21");var subQ2=makeQuery(id+"F3.opExtrude","SWEPT_EDGE",EDGE,{"disambiguationData":[OSD([subQ1,subQ0])]});Q34=makeQuery(id+"F14.opExtrude","CAP_EDGE",EDGE,{"disambiguationData":[OSD([subQ1,subQ0]),TDD([makeQuery(id+"F13.imprint","IMPRINT",EDGE,{"disambiguationData":[TD([[makeQuery(id+"F13.imprint","INTERSECT",VERTEX,{"derivedFrom":[subQ2,sQuery(id+"F13.wireOp",EDGE,"E100.bottom"),sQuery(id+"F13.wireOp",EDGE,"E100.right")]}),1.0]])],"derivedFrom":subQ2})])],"isStart":false});}
            var Q35;
            {var subQ0=sQuery(id+"F2.wireOp",EDGE,"E34");var subQ1=sQuery(id+"F2.wireOp",EDGE,"E21");var subQ2=makeQuery(id+"F3.opExtrude","SWEPT_EDGE",EDGE,{"disambiguationData":[OSD([subQ1,subQ0])]});Q35=makeQuery(id+"F14.opExtrude","CAP_EDGE",EDGE,{"disambiguationData":[OSD([subQ1,subQ0]),TDD([makeQuery(id+"F13.imprint","IMPRINT",EDGE,{"disambiguationData":[TD([[makeQuery(id+"F13.imprint","INTERSECT",VERTEX,{"derivedFrom":[subQ2,sQuery(id+"F13.wireOp",EDGE,"E102.right")]}),-1.0]])],"derivedFrom":subQ2})])],"isStart":false});}
            var Q36;
            Q36=makeQuery(id+"F14.opExtrude","CAP_EDGE",EDGE,{"disambiguationData":[OSD([sQuery(id+"F13.wireOp",EDGE,"E103.bottom")])],"isStart":false});
            var Q37;
            {var subQ0=sQuery(id+"F2.wireOp",EDGE,"E34");var subQ1=sQuery(id+"F2.wireOp",EDGE,"E21");var subQ2=makeQuery(id+"F3.opExtrude","SWEPT_EDGE",EDGE,{"disambiguationData":[OSD([subQ1,subQ0])]});Q37=makeQuery(id+"F14.opExtrude","CAP_EDGE",EDGE,{"disambiguationData":[OSD([subQ1,subQ0]),TDD([makeQuery(id+"F13.imprint","IMPRINT",EDGE,{"disambiguationData":[TD([[makeQuery(id+"F13.imprint","INTERSECT",VERTEX,{"derivedFrom":[subQ2,sQuery(id+"F13.wireOp",EDGE,"E104.left")]}),1.0]])],"derivedFrom":subQ2})])],"isStart":false});}
            var Q38;
            Q38=makeQuery(id+"F14.opExtrude","CAP_EDGE",EDGE,{"disambiguationData":[OSD([sQuery(id+"F13.wireOp",EDGE,"E105.bottom")])],"isStart":false});
            var Q39;
            {var subQ0=sQuery(id+"F2.wireOp",EDGE,"E34");var subQ1=sQuery(id+"F2.wireOp",EDGE,"E21");var subQ2=makeQuery(id+"F3.opExtrude","SWEPT_EDGE",EDGE,{"disambiguationData":[OSD([subQ1,subQ0])]});Q39=makeQuery(id+"F14.opExtrude","CAP_EDGE",EDGE,{"disambiguationData":[OSD([subQ1,subQ0]),TDD([makeQuery(id+"F13.imprint","IMPRINT",EDGE,{"disambiguationData":[TD([[makeQuery(id+"F13.imprint","INTERSECT",VERTEX,{"derivedFrom":[subQ2,sQuery(id+"F13.wireOp",EDGE,"E106.right")]}),1.0]])],"derivedFrom":subQ2})])],"isStart":false});}
            var Q40;
            {var subQ0=sQuery(id+"F2.wireOp",EDGE,"E34");var subQ1=sQuery(id+"F2.wireOp",EDGE,"E21");var subQ2=makeQuery(id+"F3.opExtrude","SWEPT_EDGE",EDGE,{"disambiguationData":[OSD([subQ1,subQ0])]});Q40=makeQuery(id+"F14.opExtrude","CAP_EDGE",EDGE,{"disambiguationData":[OSD([subQ1,subQ0]),TDD([makeQuery(id+"F13.imprint","IMPRINT",EDGE,{"disambiguationData":[TD([[makeQuery(id+"F13.imprint","INTERSECT",VERTEX,{"derivedFrom":[subQ2,sQuery(id+"F13.wireOp",EDGE,"E107.bottom"),sQuery(id+"F13.wireOp",EDGE,"E107.right")]}),1.0]])],"derivedFrom":subQ2})])],"isStart":false});}
            var Q41;
            {var subQ0=sQuery(id+"F2.wireOp",EDGE,"E34");var subQ1=sQuery(id+"F2.wireOp",EDGE,"E21");var subQ2=makeQuery(id+"F3.opExtrude","SWEPT_EDGE",EDGE,{"disambiguationData":[OSD([subQ1,subQ0])]});Q41=makeQuery(id+"F14.opExtrude","CAP_EDGE",EDGE,{"disambiguationData":[OSD([subQ1,subQ0]),TDD([makeQuery(id+"F13.imprint","IMPRINT",EDGE,{"disambiguationData":[TD([[makeQuery(id+"F13.imprint","INTERSECT",VERTEX,{"derivedFrom":[subQ2,sQuery(id+"F13.wireOp",EDGE,"E108.bottom"),sQuery(id+"F13.wireOp",EDGE,"E108.right")]}),1.0]])],"derivedFrom":subQ2})])],"isStart":false});}
            var Q42;
            {var subQ0=sQuery(id+"F2.wireOp",EDGE,"E34");var subQ1=sQuery(id+"F2.wireOp",EDGE,"E21");var subQ2=makeQuery(id+"F3.opExtrude","SWEPT_EDGE",EDGE,{"disambiguationData":[OSD([subQ1,subQ0])]});Q42=makeQuery(id+"F14.opExtrude","CAP_EDGE",EDGE,{"disambiguationData":[OSD([subQ1,subQ0]),TDD([makeQuery(id+"F13.imprint","IMPRINT",EDGE,{"disambiguationData":[TD([[makeQuery(id+"F13.imprint","INTERSECT",VERTEX,{"derivedFrom":[subQ2,sQuery(id+"F13.wireOp",EDGE,"E110.right")]}),-1.0]])],"derivedFrom":subQ2})])],"isStart":false});}
            var Q43;
            Q43=makeQuery(id+"F14.opExtrude","CAP_EDGE",EDGE,{"disambiguationData":[OSD([sQuery(id+"F13.wireOp",EDGE,"E111.bottom")])],"isStart":false});
            var Q44;
            {var subQ0=sQuery(id+"F2.wireOp",EDGE,"E29");var subQ1=sQuery(id+"F2.wireOp",EDGE,"E12");var subQ2=makeQuery(id+"F3.opExtrude","SWEPT_EDGE",EDGE,{"disambiguationData":[OSD([subQ1,subQ0])]});Q44=makeQuery(id+"F16.opExtrude","CAP_EDGE",EDGE,{"disambiguationData":[OSD([subQ1,subQ0]),TDD([makeQuery(id+"F15.imprint","IMPRINT",EDGE,{"disambiguationData":[TD([[makeQuery(id+"F15.imprint","INTERSECT",VERTEX,{"derivedFrom":[subQ2,sQuery(id+"F15.wireOp",EDGE,"E162.right")]}),1.0]])],"derivedFrom":subQ2})])],"isStart":false});}
            var Q45;
            {var subQ0=sQuery(id+"F2.wireOp",EDGE,"E29");var subQ1=sQuery(id+"F2.wireOp",EDGE,"E12");var subQ2=makeQuery(id+"F3.opExtrude","SWEPT_EDGE",EDGE,{"disambiguationData":[OSD([subQ1,subQ0])]});Q45=makeQuery(id+"F16.opExtrude","CAP_EDGE",EDGE,{"disambiguationData":[OSD([subQ1,subQ0]),TDD([makeQuery(id+"F15.imprint","IMPRINT",EDGE,{"disambiguationData":[TD([[makeQuery(id+"F15.imprint","INTERSECT",VERTEX,{"derivedFrom":[subQ2,sQuery(id+"F15.wireOp",EDGE,"E161.right")]}),1.0]])],"derivedFrom":subQ2})])],"isStart":false});}
            var Q46;
            {var subQ0=sQuery(id+"F2.wireOp",EDGE,"E29");var subQ1=sQuery(id+"F2.wireOp",EDGE,"E12");var subQ2=makeQuery(id+"F3.opExtrude","SWEPT_EDGE",EDGE,{"disambiguationData":[OSD([subQ1,subQ0])]});Q46=makeQuery(id+"F16.opExtrude","CAP_EDGE",EDGE,{"disambiguationData":[OSD([subQ1,subQ0]),TDD([makeQuery(id+"F15.imprint","IMPRINT",EDGE,{"disambiguationData":[TD([[makeQuery(id+"F15.imprint","INTERSECT",VERTEX,{"derivedFrom":[subQ2,sQuery(id+"F15.wireOp",EDGE,"E159.right")]}),-1.0]])],"derivedFrom":subQ2})])],"isStart":false});}
            var Q47;
            {var subQ0=sQuery(id+"F2.wireOp",EDGE,"E29");var subQ1=sQuery(id+"F2.wireOp",EDGE,"E12");var subQ2=makeQuery(id+"F3.opExtrude","SWEPT_EDGE",EDGE,{"disambiguationData":[OSD([subQ1,subQ0])]});Q47=makeQuery(id+"F16.opExtrude","CAP_EDGE",EDGE,{"disambiguationData":[OSD([subQ1,subQ0]),TDD([makeQuery(id+"F15.imprint","IMPRINT",EDGE,{"disambiguationData":[TD([[makeQuery(id+"F15.imprint","INTERSECT",VERTEX,{"derivedFrom":[subQ2,sQuery(id+"F15.wireOp",EDGE,"E158.right")]}),-1.0]])],"derivedFrom":subQ2})])],"isStart":false});}
            var Q48;
            {var subQ0=sQuery(id+"F2.wireOp",EDGE,"E29");var subQ1=sQuery(id+"F2.wireOp",EDGE,"E12");var subQ2=makeQuery(id+"F3.opExtrude","SWEPT_EDGE",EDGE,{"disambiguationData":[OSD([subQ1,subQ0])]});Q48=makeQuery(id+"F16.opExtrude","CAP_EDGE",EDGE,{"disambiguationData":[OSD([subQ1,subQ0]),TDD([makeQuery(id+"F15.imprint","IMPRINT",EDGE,{"disambiguationData":[TD([[makeQuery(id+"F15.imprint","INTERSECT",VERTEX,{"derivedFrom":[subQ2,sQuery(id+"F15.wireOp",EDGE,"E157.right")]}),-1.0]])],"derivedFrom":subQ2})])],"isStart":false});}
            var Q49;
            {var subQ0=sQuery(id+"F2.wireOp",EDGE,"E29");var subQ1=sQuery(id+"F2.wireOp",EDGE,"E12");var subQ2=makeQuery(id+"F3.opExtrude","SWEPT_EDGE",EDGE,{"disambiguationData":[OSD([subQ1,subQ0])]});Q49=makeQuery(id+"F16.opExtrude","CAP_EDGE",EDGE,{"disambiguationData":[OSD([subQ1,subQ0]),TDD([makeQuery(id+"F15.imprint","IMPRINT",EDGE,{"disambiguationData":[TD([[makeQuery(id+"F15.imprint","INTERSECT",VERTEX,{"derivedFrom":[subQ2,sQuery(id+"F15.wireOp",EDGE,"E156.left")]}),-1.0]])],"derivedFrom":subQ2})])],"isStart":false});}
            var Q50;
            {var subQ0=sQuery(id+"F2.wireOp",EDGE,"E29");var subQ1=sQuery(id+"F2.wireOp",EDGE,"E12");var subQ2=makeQuery(id+"F3.opExtrude","SWEPT_EDGE",EDGE,{"disambiguationData":[OSD([subQ1,subQ0])]});Q50=makeQuery(id+"F16.opExtrude","CAP_EDGE",EDGE,{"disambiguationData":[OSD([subQ1,subQ0]),TDD([makeQuery(id+"F15.imprint","IMPRINT",EDGE,{"disambiguationData":[TD([[makeQuery(id+"F15.imprint","INTERSECT",VERTEX,{"derivedFrom":[subQ2,sQuery(id+"F15.wireOp",EDGE,"E155.left")]}),-1.0]])],"derivedFrom":subQ2})])],"isStart":false});}
            var Q51;
            {var subQ0=sQuery(id+"F2.wireOp",EDGE,"E29");var subQ1=sQuery(id+"F2.wireOp",EDGE,"E12");var subQ2=makeQuery(id+"F3.opExtrude","SWEPT_EDGE",EDGE,{"disambiguationData":[OSD([subQ1,subQ0])]});Q51=makeQuery(id+"F16.opExtrude","CAP_EDGE",EDGE,{"disambiguationData":[OSD([subQ1,subQ0]),TDD([makeQuery(id+"F15.imprint","IMPRINT",EDGE,{"disambiguationData":[TD([[makeQuery(id+"F15.imprint","INTERSECT",VERTEX,{"derivedFrom":[subQ2,sQuery(id+"F15.wireOp",EDGE,"E154.left")]}),-1.0]])],"derivedFrom":subQ2})])],"isStart":false});}
            var Q52;
            {var subQ0=sQuery(id+"F2.wireOp",EDGE,"E29");var subQ1=sQuery(id+"F2.wireOp",EDGE,"E12");var subQ2=makeQuery(id+"F3.opExtrude","SWEPT_EDGE",EDGE,{"disambiguationData":[OSD([subQ1,subQ0])]});Q52=makeQuery(id+"F16.opExtrude","CAP_EDGE",EDGE,{"disambiguationData":[OSD([subQ1,subQ0]),TDD([makeQuery(id+"F15.imprint","IMPRINT",EDGE,{"disambiguationData":[TD([[makeQuery(id+"F15.imprint","INTERSECT",VERTEX,{"derivedFrom":[subQ2,sQuery(id+"F15.wireOp",EDGE,"E153.right")]}),1.0]])],"derivedFrom":subQ2})])],"isStart":false});}
            var Q53;
            {var subQ0=sQuery(id+"F2.wireOp",EDGE,"E29");var subQ1=sQuery(id+"F2.wireOp",EDGE,"E12");var subQ2=makeQuery(id+"F3.opExtrude","SWEPT_EDGE",EDGE,{"disambiguationData":[OSD([subQ1,subQ0])]});Q53=makeQuery(id+"F16.opExtrude","CAP_EDGE",EDGE,{"disambiguationData":[OSD([subQ1,subQ0]),TDD([makeQuery(id+"F15.imprint","IMPRINT",EDGE,{"disambiguationData":[TD([[makeQuery(id+"F15.imprint","INTERSECT",VERTEX,{"derivedFrom":[subQ2,sQuery(id+"F15.wireOp",EDGE,"E151.right")]}),-1.0]])],"derivedFrom":subQ2})])],"isStart":false});}
            var Q54;
            {var subQ0=sQuery(id+"F2.wireOp",EDGE,"E29");var subQ1=sQuery(id+"F2.wireOp",EDGE,"E12");var subQ2=makeQuery(id+"F3.opExtrude","SWEPT_EDGE",EDGE,{"disambiguationData":[OSD([subQ1,subQ0])]});Q54=makeQuery(id+"F16.opExtrude","CAP_EDGE",EDGE,{"disambiguationData":[OSD([subQ1,subQ0]),TDD([makeQuery(id+"F15.imprint","IMPRINT",EDGE,{"disambiguationData":[TD([[makeQuery(id+"F15.imprint","INTERSECT",VERTEX,{"derivedFrom":[subQ2,sQuery(id+"F15.wireOp",EDGE,"E150.right")]}),-1.0]])],"derivedFrom":subQ2})])],"isStart":false});}
            var Q55;
            {var subQ0=sQuery(id+"F2.wireOp",EDGE,"E29");var subQ1=sQuery(id+"F2.wireOp",EDGE,"E12");var subQ2=makeQuery(id+"F3.opExtrude","SWEPT_EDGE",EDGE,{"disambiguationData":[OSD([subQ1,subQ0])]});Q55=makeQuery(id+"F16.opExtrude","CAP_EDGE",EDGE,{"disambiguationData":[OSD([subQ1,subQ0]),TDD([makeQuery(id+"F15.imprint","IMPRINT",EDGE,{"disambiguationData":[TD([[makeQuery(id+"F15.imprint","INTERSECT",VERTEX,{"derivedFrom":[subQ2,sQuery(id+"F15.wireOp",EDGE,"E149.right")]}),-1.0]])],"derivedFrom":subQ2})])],"isStart":false});}
            var Q56;
            {var subQ0=sQuery(id+"F2.wireOp",EDGE,"E29");var subQ1=sQuery(id+"F2.wireOp",EDGE,"E12");var subQ2=makeQuery(id+"F3.opExtrude","SWEPT_EDGE",EDGE,{"disambiguationData":[OSD([subQ1,subQ0])]});Q56=makeQuery(id+"F16.opExtrude","CAP_EDGE",EDGE,{"disambiguationData":[OSD([subQ1,subQ0]),TDD([makeQuery(id+"F15.imprint","IMPRINT",EDGE,{"disambiguationData":[TD([[makeQuery(id+"F15.imprint","INTERSECT",VERTEX,{"derivedFrom":[subQ2,sQuery(id+"F15.wireOp",EDGE,"E148.left")]}),-1.0]])],"derivedFrom":subQ2})])],"isStart":false});}
            var Q57;
            {var subQ0=sQuery(id+"F2.wireOp",EDGE,"E29");var subQ1=sQuery(id+"F2.wireOp",EDGE,"E12");var subQ2=makeQuery(id+"F3.opExtrude","SWEPT_EDGE",EDGE,{"disambiguationData":[OSD([subQ1,subQ0])]});Q57=makeQuery(id+"F16.opExtrude","CAP_EDGE",EDGE,{"disambiguationData":[OSD([subQ1,subQ0]),TDD([makeQuery(id+"F15.imprint","IMPRINT",EDGE,{"disambiguationData":[TD([[makeQuery(id+"F15.imprint","INTERSECT",VERTEX,{"derivedFrom":[subQ2,sQuery(id+"F15.wireOp",EDGE,"E147.left")]}),-1.0]])],"derivedFrom":subQ2})])],"isStart":false});}
            var Q58;
            {var subQ0=sQuery(id+"F2.wireOp",EDGE,"E29");var subQ1=sQuery(id+"F2.wireOp",EDGE,"E12");var subQ2=makeQuery(id+"F3.opExtrude","SWEPT_EDGE",EDGE,{"disambiguationData":[OSD([subQ1,subQ0])]});Q58=makeQuery(id+"F16.opExtrude","CAP_EDGE",EDGE,{"disambiguationData":[OSD([subQ1,subQ0]),TDD([makeQuery(id+"F15.imprint","IMPRINT",EDGE,{"disambiguationData":[TD([[makeQuery(id+"F15.imprint","INTERSECT",VERTEX,{"derivedFrom":[subQ2,sQuery(id+"F15.wireOp",EDGE,"E146.left")]}),-1.0]])],"derivedFrom":subQ2})])],"isStart":false});}
            var Q59;
            {var subQ0=sQuery(id+"F2.wireOp",EDGE,"E29");var subQ1=sQuery(id+"F2.wireOp",EDGE,"E12");var subQ2=makeQuery(id+"F3.opExtrude","SWEPT_EDGE",EDGE,{"disambiguationData":[OSD([subQ1,subQ0])]});Q59=makeQuery(id+"F16.opExtrude","CAP_EDGE",EDGE,{"disambiguationData":[OSD([subQ1,subQ0]),TDD([makeQuery(id+"F15.imprint","IMPRINT",EDGE,{"disambiguationData":[TD([[makeQuery(id+"F15.imprint","INTERSECT",VERTEX,{"derivedFrom":[subQ2,sQuery(id+"F15.wireOp",EDGE,"E145.right")]}),1.0]])],"derivedFrom":subQ2})])],"isStart":false});}
            var Q60;
            {var subQ0=sQuery(id+"F2.wireOp",EDGE,"E29");var subQ1=sQuery(id+"F2.wireOp",EDGE,"E12");var subQ2=makeQuery(id+"F3.opExtrude","SWEPT_EDGE",EDGE,{"disambiguationData":[OSD([subQ1,subQ0])]});Q60=makeQuery(id+"F16.opExtrude","CAP_EDGE",EDGE,{"disambiguationData":[OSD([subQ1,subQ0]),TDD([makeQuery(id+"F15.imprint","IMPRINT",EDGE,{"disambiguationData":[TD([[makeQuery(id+"F15.imprint","INTERSECT",VERTEX,{"derivedFrom":[subQ2,sQuery(id+"F15.wireOp",EDGE,"E143.right")]}),-1.0]])],"derivedFrom":subQ2})])],"isStart":false});}
            var Q61;
            {var subQ0=sQuery(id+"F2.wireOp",EDGE,"E29");var subQ1=sQuery(id+"F2.wireOp",EDGE,"E12");var subQ2=makeQuery(id+"F3.opExtrude","SWEPT_EDGE",EDGE,{"disambiguationData":[OSD([subQ1,subQ0])]});Q61=makeQuery(id+"F16.opExtrude","CAP_EDGE",EDGE,{"disambiguationData":[OSD([subQ1,subQ0]),TDD([makeQuery(id+"F15.imprint","IMPRINT",EDGE,{"disambiguationData":[TD([[makeQuery(id+"F15.imprint","INTERSECT",VERTEX,{"derivedFrom":[subQ2,sQuery(id+"F15.wireOp",EDGE,"E142.right")]}),-1.0]])],"derivedFrom":subQ2})])],"isStart":false});}
            var Q62;
            {var subQ0=sQuery(id+"F2.wireOp",EDGE,"E29");var subQ1=sQuery(id+"F2.wireOp",EDGE,"E12");var subQ2=makeQuery(id+"F3.opExtrude","SWEPT_EDGE",EDGE,{"disambiguationData":[OSD([subQ1,subQ0])]});Q62=makeQuery(id+"F16.opExtrude","CAP_EDGE",EDGE,{"disambiguationData":[OSD([subQ1,subQ0]),TDD([makeQuery(id+"F15.imprint","IMPRINT",EDGE,{"disambiguationData":[TD([[makeQuery(id+"F15.imprint","INTERSECT",VERTEX,{"derivedFrom":[subQ2,sQuery(id+"F15.wireOp",EDGE,"E141.left")]}),-1.0]])],"derivedFrom":subQ2})])],"isStart":false});}
            var Q63;
            {var subQ0=sQuery(id+"F2.wireOp",EDGE,"E29");var subQ1=sQuery(id+"F2.wireOp",EDGE,"E12");var subQ2=makeQuery(id+"F3.opExtrude","SWEPT_EDGE",EDGE,{"disambiguationData":[OSD([subQ1,subQ0])]});Q63=makeQuery(id+"F16.opExtrude","CAP_EDGE",EDGE,{"disambiguationData":[OSD([subQ1,subQ0]),TDD([makeQuery(id+"F15.imprint","IMPRINT",EDGE,{"disambiguationData":[TD([[makeQuery(id+"F15.imprint","INTERSECT",VERTEX,{"derivedFrom":[subQ2,sQuery(id+"F15.wireOp",EDGE,"E140.left")]}),-1.0]])],"derivedFrom":subQ2})])],"isStart":false});}
            var Q64;
            {var subQ0=sQuery(id+"F2.wireOp",EDGE,"E29");var subQ1=sQuery(id+"F2.wireOp",EDGE,"E12");var subQ2=makeQuery(id+"F3.opExtrude","SWEPT_EDGE",EDGE,{"disambiguationData":[OSD([subQ1,subQ0])]});Q64=makeQuery(id+"F16.opExtrude","CAP_EDGE",EDGE,{"disambiguationData":[OSD([subQ1,subQ0]),TDD([makeQuery(id+"F15.imprint","IMPRINT",EDGE,{"disambiguationData":[TD([[makeQuery(id+"F15.imprint","INTERSECT",VERTEX,{"derivedFrom":[subQ2,sQuery(id+"F15.wireOp",EDGE,"E139.left")]}),-1.0]])],"derivedFrom":subQ2})])],"isStart":false});}
            var Q65;
            {var subQ0=sQuery(id+"F2.wireOp",EDGE,"E29");var subQ1=sQuery(id+"F2.wireOp",EDGE,"E12");var subQ2=makeQuery(id+"F3.opExtrude","SWEPT_EDGE",EDGE,{"disambiguationData":[OSD([subQ1,subQ0])]});Q65=makeQuery(id+"F16.opExtrude","CAP_EDGE",EDGE,{"disambiguationData":[OSD([subQ1,subQ0]),TDD([makeQuery(id+"F15.imprint","IMPRINT",EDGE,{"disambiguationData":[TD([[makeQuery(id+"F15.imprint","INTERSECT",VERTEX,{"derivedFrom":[subQ2,sQuery(id+"F15.wireOp",EDGE,"E138.right")]}),1.0]])],"derivedFrom":subQ2})])],"isStart":false});}
            var Q66;
            {var subQ0=sQuery(id+"F2.wireOp",EDGE,"E29");var subQ1=sQuery(id+"F2.wireOp",EDGE,"E12");var subQ2=makeQuery(id+"F3.opExtrude","SWEPT_EDGE",EDGE,{"disambiguationData":[OSD([subQ1,subQ0])]});Q66=makeQuery(id+"F16.opExtrude","CAP_EDGE",EDGE,{"disambiguationData":[OSD([subQ1,subQ0]),TDD([makeQuery(id+"F15.imprint","IMPRINT",EDGE,{"disambiguationData":[TD([[makeQuery(id+"F15.imprint","INTERSECT",VERTEX,{"derivedFrom":[subQ2,sQuery(id+"F15.wireOp",EDGE,"E136.right")]}),-1.0]])],"derivedFrom":subQ2})])],"isStart":false});}
            var Q67;
            {var subQ0=sQuery(id+"F2.wireOp",EDGE,"E29");var subQ1=sQuery(id+"F2.wireOp",EDGE,"E12");var subQ2=makeQuery(id+"F3.opExtrude","SWEPT_EDGE",EDGE,{"disambiguationData":[OSD([subQ1,subQ0])]});Q67=makeQuery(id+"F16.opExtrude","CAP_EDGE",EDGE,{"disambiguationData":[OSD([subQ1,subQ0]),TDD([makeQuery(id+"F15.imprint","IMPRINT",EDGE,{"disambiguationData":[TD([[makeQuery(id+"F15.imprint","INTERSECT",VERTEX,{"derivedFrom":[subQ2,sQuery(id+"F15.wireOp",EDGE,"E135.right")]}),-1.0]])],"derivedFrom":subQ2})])],"isStart":false});}
            var Q68;
            {var subQ0=sQuery(id+"F2.wireOp",EDGE,"E29");var subQ1=sQuery(id+"F2.wireOp",EDGE,"E12");var subQ2=makeQuery(id+"F3.opExtrude","SWEPT_EDGE",EDGE,{"disambiguationData":[OSD([subQ1,subQ0])]});Q68=makeQuery(id+"F16.opExtrude","CAP_EDGE",EDGE,{"disambiguationData":[OSD([subQ1,subQ0]),TDD([makeQuery(id+"F15.imprint","IMPRINT",EDGE,{"disambiguationData":[TD([[makeQuery(id+"F15.imprint","INTERSECT",VERTEX,{"derivedFrom":[subQ2,sQuery(id+"F15.wireOp",EDGE,"E134.right")]}),-1.0]])],"derivedFrom":subQ2})])],"isStart":false});}
            var Q69;
            {var subQ0=sQuery(id+"F2.wireOp",EDGE,"E29");var subQ1=sQuery(id+"F2.wireOp",EDGE,"E12");var subQ2=makeQuery(id+"F3.opExtrude","SWEPT_EDGE",EDGE,{"disambiguationData":[OSD([subQ1,subQ0])]});Q69=makeQuery(id+"F16.opExtrude","CAP_EDGE",EDGE,{"disambiguationData":[OSD([subQ1,subQ0]),TDD([makeQuery(id+"F15.imprint","IMPRINT",EDGE,{"disambiguationData":[TD([[makeQuery(id+"F15.imprint","INTERSECT",VERTEX,{"derivedFrom":[subQ2,sQuery(id+"F15.wireOp",EDGE,"E133.left")]}),-1.0]])],"derivedFrom":subQ2})])],"isStart":false});}
            var Q70;
            {var subQ0=sQuery(id+"F2.wireOp",EDGE,"E29");var subQ1=sQuery(id+"F2.wireOp",EDGE,"E12");var subQ2=makeQuery(id+"F3.opExtrude","SWEPT_EDGE",EDGE,{"disambiguationData":[OSD([subQ1,subQ0])]});Q70=makeQuery(id+"F16.opExtrude","CAP_EDGE",EDGE,{"disambiguationData":[OSD([subQ1,subQ0]),TDD([makeQuery(id+"F15.imprint","IMPRINT",EDGE,{"disambiguationData":[TD([[makeQuery(id+"F15.imprint","INTERSECT",VERTEX,{"derivedFrom":[subQ2,sQuery(id+"F15.wireOp",EDGE,"E132.left")]}),-1.0]])],"derivedFrom":subQ2})])],"isStart":false});}
            var Q71;
            {var subQ0=sQuery(id+"F2.wireOp",EDGE,"E29");var subQ1=sQuery(id+"F2.wireOp",EDGE,"E12");var subQ2=makeQuery(id+"F3.opExtrude","SWEPT_EDGE",EDGE,{"disambiguationData":[OSD([subQ1,subQ0])]});Q71=makeQuery(id+"F16.opExtrude","CAP_EDGE",EDGE,{"disambiguationData":[OSD([subQ1,subQ0]),TDD([makeQuery(id+"F15.imprint","IMPRINT",EDGE,{"disambiguationData":[TD([[makeQuery(id+"F15.imprint","INTERSECT",VERTEX,{"derivedFrom":[subQ2,sQuery(id+"F15.wireOp",EDGE,"E131.left")]}),-1.0]])],"derivedFrom":subQ2})])],"isStart":false});}
            var Q72;
            {var subQ0=sQuery(id+"F2.wireOp",EDGE,"E29");var subQ1=sQuery(id+"F2.wireOp",EDGE,"E12");var subQ2=makeQuery(id+"F3.opExtrude","SWEPT_EDGE",EDGE,{"disambiguationData":[OSD([subQ1,subQ0])]});Q72=makeQuery(id+"F16.opExtrude","CAP_EDGE",EDGE,{"disambiguationData":[OSD([subQ1,subQ0]),TDD([makeQuery(id+"F15.imprint","IMPRINT",EDGE,{"disambiguationData":[TD([[makeQuery(id+"F15.imprint","INTERSECT",VERTEX,{"derivedFrom":[subQ2,sQuery(id+"F15.wireOp",EDGE,"E130.right")]}),1.0]])],"derivedFrom":subQ2})])],"isStart":false});}
            var Q73;
            {var subQ0=sQuery(id+"F2.wireOp",EDGE,"E29");var subQ1=sQuery(id+"F2.wireOp",EDGE,"E12");var subQ2=makeQuery(id+"F3.opExtrude","SWEPT_EDGE",EDGE,{"disambiguationData":[OSD([subQ1,subQ0])]});Q73=makeQuery(id+"F16.opExtrude","CAP_EDGE",EDGE,{"disambiguationData":[OSD([subQ1,subQ0]),TDD([makeQuery(id+"F15.imprint","IMPRINT",EDGE,{"disambiguationData":[TD([[makeQuery(id+"F15.imprint","INTERSECT",VERTEX,{"derivedFrom":[subQ2,sQuery(id+"F15.wireOp",EDGE,"E128.right")]}),-1.0]])],"derivedFrom":subQ2})])],"isStart":false});}
            var Q74;
            {var subQ0=sQuery(id+"F2.wireOp",EDGE,"E29");var subQ1=sQuery(id+"F2.wireOp",EDGE,"E12");var subQ2=makeQuery(id+"F3.opExtrude","SWEPT_EDGE",EDGE,{"disambiguationData":[OSD([subQ1,subQ0])]});Q74=makeQuery(id+"F16.opExtrude","CAP_EDGE",EDGE,{"disambiguationData":[OSD([subQ1,subQ0]),TDD([makeQuery(id+"F15.imprint","IMPRINT",EDGE,{"disambiguationData":[TD([[makeQuery(id+"F15.imprint","INTERSECT",VERTEX,{"derivedFrom":[subQ2,sQuery(id+"F15.wireOp",EDGE,"E127.right")]}),-1.0]])],"derivedFrom":subQ2})])],"isStart":false});}
            var Q75;
            {var subQ0=sQuery(id+"F2.wireOp",EDGE,"E29");var subQ1=sQuery(id+"F2.wireOp",EDGE,"E12");var subQ2=makeQuery(id+"F3.opExtrude","SWEPT_EDGE",EDGE,{"disambiguationData":[OSD([subQ1,subQ0])]});Q75=makeQuery(id+"F16.opExtrude","CAP_EDGE",EDGE,{"disambiguationData":[OSD([subQ1,subQ0]),TDD([makeQuery(id+"F15.imprint","IMPRINT",EDGE,{"disambiguationData":[TD([[makeQuery(id+"F15.imprint","INTERSECT",VERTEX,{"derivedFrom":[subQ2,sQuery(id+"F15.wireOp",EDGE,"E126.right")]}),-1.0]])],"derivedFrom":subQ2})])],"isStart":false});}
            var Q76;
            {var subQ0=sQuery(id+"F2.wireOp",EDGE,"E29");var subQ1=sQuery(id+"F2.wireOp",EDGE,"E12");var subQ2=makeQuery(id+"F3.opExtrude","SWEPT_EDGE",EDGE,{"disambiguationData":[OSD([subQ1,subQ0])]});Q76=makeQuery(id+"F16.opExtrude","CAP_EDGE",EDGE,{"disambiguationData":[OSD([subQ1,subQ0]),TDD([makeQuery(id+"F15.imprint","IMPRINT",EDGE,{"disambiguationData":[TD([[makeQuery(id+"F15.imprint","INTERSECT",VERTEX,{"derivedFrom":[subQ2,sQuery(id+"F15.wireOp",EDGE,"E125.left")]}),-1.0]])],"derivedFrom":subQ2})])],"isStart":false});}
            var Q77;
            {var subQ0=sQuery(id+"F2.wireOp",EDGE,"E29");var subQ1=sQuery(id+"F2.wireOp",EDGE,"E12");var subQ2=makeQuery(id+"F3.opExtrude","SWEPT_EDGE",EDGE,{"disambiguationData":[OSD([subQ1,subQ0])]});Q77=makeQuery(id+"F16.opExtrude","CAP_EDGE",EDGE,{"disambiguationData":[OSD([subQ1,subQ0]),TDD([makeQuery(id+"F15.imprint","IMPRINT",EDGE,{"disambiguationData":[TD([[makeQuery(id+"F15.imprint","INTERSECT",VERTEX,{"derivedFrom":[subQ2,sQuery(id+"F15.wireOp",EDGE,"E124.left")]}),-1.0]])],"derivedFrom":subQ2})])],"isStart":false});}
            var Q78;
            {var subQ0=sQuery(id+"F2.wireOp",EDGE,"E29");var subQ1=sQuery(id+"F2.wireOp",EDGE,"E12");var subQ2=makeQuery(id+"F3.opExtrude","SWEPT_EDGE",EDGE,{"disambiguationData":[OSD([subQ1,subQ0])]});Q78=makeQuery(id+"F16.opExtrude","CAP_EDGE",EDGE,{"disambiguationData":[OSD([subQ1,subQ0]),TDD([makeQuery(id+"F15.imprint","IMPRINT",EDGE,{"disambiguationData":[TD([[makeQuery(id+"F15.imprint","INTERSECT",VERTEX,{"derivedFrom":[subQ2,sQuery(id+"F15.wireOp",EDGE,"E123.left")]}),-1.0]])],"derivedFrom":subQ2})])],"isStart":false});}
            var Q79;
            {var subQ0=sQuery(id+"F2.wireOp",EDGE,"E29");var subQ1=sQuery(id+"F2.wireOp",EDGE,"E12");var subQ2=makeQuery(id+"F3.opExtrude","SWEPT_EDGE",EDGE,{"disambiguationData":[OSD([subQ1,subQ0])]});Q79=makeQuery(id+"F16.opExtrude","CAP_EDGE",EDGE,{"disambiguationData":[OSD([subQ1,subQ0]),TDD([makeQuery(id+"F15.imprint","IMPRINT",EDGE,{"disambiguationData":[TD([[makeQuery(id+"F15.imprint","INTERSECT",VERTEX,{"derivedFrom":[subQ2,sQuery(id+"F15.wireOp",EDGE,"E122.right")]}),1.0]])],"derivedFrom":subQ2})])],"isStart":false});}
            var Q80;
            {var subQ0=sQuery(id+"F2.wireOp",EDGE,"E29");var subQ1=sQuery(id+"F2.wireOp",EDGE,"E12");var subQ2=makeQuery(id+"F3.opExtrude","SWEPT_EDGE",EDGE,{"disambiguationData":[OSD([subQ1,subQ0])]});Q80=makeQuery(id+"F16.opExtrude","CAP_EDGE",EDGE,{"disambiguationData":[OSD([subQ1,subQ0]),TDD([makeQuery(id+"F15.imprint","IMPRINT",EDGE,{"disambiguationData":[TD([[makeQuery(id+"F15.imprint","INTERSECT",VERTEX,{"derivedFrom":[subQ2,sQuery(id+"F15.wireOp",EDGE,"E120.right")]}),-1.0]])],"derivedFrom":subQ2})])],"isStart":false});}
            var Q81;
            {var subQ0=sQuery(id+"F2.wireOp",EDGE,"E29");var subQ1=sQuery(id+"F2.wireOp",EDGE,"E12");var subQ2=makeQuery(id+"F3.opExtrude","SWEPT_EDGE",EDGE,{"disambiguationData":[OSD([subQ1,subQ0])]});Q81=makeQuery(id+"F16.opExtrude","CAP_EDGE",EDGE,{"disambiguationData":[OSD([subQ1,subQ0]),TDD([makeQuery(id+"F15.imprint","IMPRINT",EDGE,{"disambiguationData":[TD([[makeQuery(id+"F15.imprint","INTERSECT",VERTEX,{"derivedFrom":[subQ2,sQuery(id+"F15.wireOp",EDGE,"E119.right")]}),-1.0]])],"derivedFrom":subQ2})])],"isStart":false});}
            var Q82;
            {var subQ0=sQuery(id+"F2.wireOp",EDGE,"E29");var subQ1=sQuery(id+"F2.wireOp",EDGE,"E12");var subQ2=makeQuery(id+"F3.opExtrude","SWEPT_EDGE",EDGE,{"disambiguationData":[OSD([subQ1,subQ0])]});Q82=makeQuery(id+"F16.opExtrude","CAP_EDGE",EDGE,{"disambiguationData":[OSD([subQ1,subQ0]),TDD([makeQuery(id+"F15.imprint","IMPRINT",EDGE,{"disambiguationData":[TD([[makeQuery(id+"F15.imprint","INTERSECT",VERTEX,{"derivedFrom":[subQ2,sQuery(id+"F15.wireOp",EDGE,"E117.left")]}),-1.0]])],"derivedFrom":subQ2})])],"isStart":false});}
            var Q83;
            {var subQ0=sQuery(id+"F2.wireOp",EDGE,"E29");var subQ1=sQuery(id+"F2.wireOp",EDGE,"E12");var subQ2=makeQuery(id+"F3.opExtrude","SWEPT_EDGE",EDGE,{"disambiguationData":[OSD([subQ1,subQ0])]});Q83=makeQuery(id+"F16.opExtrude","CAP_EDGE",EDGE,{"disambiguationData":[OSD([subQ1,subQ0]),TDD([makeQuery(id+"F15.imprint","IMPRINT",EDGE,{"disambiguationData":[TD([[makeQuery(id+"F15.imprint","INTERSECT",VERTEX,{"derivedFrom":[subQ2,sQuery(id+"F15.wireOp",EDGE,"E118.right")]}),-1.0]])],"derivedFrom":subQ2})])],"isStart":false});}
            var Q84;
            {var subQ0=sQuery(id+"F2.wireOp",EDGE,"E29");var subQ1=sQuery(id+"F2.wireOp",EDGE,"E12");var subQ2=makeQuery(id+"F3.opExtrude","SWEPT_EDGE",EDGE,{"disambiguationData":[OSD([subQ1,subQ0])]});Q84=makeQuery(id+"F16.opExtrude","CAP_EDGE",EDGE,{"disambiguationData":[OSD([subQ1,subQ0]),TDD([makeQuery(id+"F15.imprint","IMPRINT",EDGE,{"disambiguationData":[TD([[makeQuery(id+"F15.imprint","INTERSECT",VERTEX,{"derivedFrom":[subQ2,sQuery(id+"F15.wireOp",EDGE,"E116.left")]}),-1.0]])],"derivedFrom":subQ2})])],"isStart":false});}
            var Q85;
            {var subQ0=sQuery(id+"F2.wireOp",EDGE,"E29");var subQ1=sQuery(id+"F2.wireOp",EDGE,"E12");var subQ2=makeQuery(id+"F3.opExtrude","SWEPT_EDGE",EDGE,{"disambiguationData":[OSD([subQ1,subQ0])]});Q85=makeQuery(id+"F16.opExtrude","CAP_EDGE",EDGE,{"disambiguationData":[OSD([subQ1,subQ0]),TDD([makeQuery(id+"F15.imprint","IMPRINT",EDGE,{"disambiguationData":[TD([[makeQuery(id+"F15.imprint","INTERSECT",VERTEX,{"derivedFrom":[subQ2,sQuery(id+"F15.wireOp",EDGE,"E115.left")]}),-1.0]])],"derivedFrom":subQ2})])],"isStart":false});}
            var Q86;
            {var subQ0=sQuery(id+"F2.wireOp",EDGE,"E29");var subQ1=sQuery(id+"F2.wireOp",EDGE,"E12");var subQ2=makeQuery(id+"F3.opExtrude","SWEPT_EDGE",EDGE,{"disambiguationData":[OSD([subQ1,subQ0])]});Q86=makeQuery(id+"F16.opExtrude","CAP_EDGE",EDGE,{"disambiguationData":[OSD([subQ1,subQ0]),TDD([makeQuery(id+"F15.imprint","IMPRINT",EDGE,{"disambiguationData":[TD([[makeQuery(id+"F15.imprint","INTERSECT",VERTEX,{"derivedFrom":[subQ2,sQuery(id+"F15.wireOp",EDGE,"E114.right")]}),1.0]])],"derivedFrom":subQ2})])],"isStart":false});}
            var Q87;
            {var subQ0=sQuery(id+"F2.wireOp",EDGE,"E29");var subQ1=sQuery(id+"F2.wireOp",EDGE,"E12");var subQ2=makeQuery(id+"F3.opExtrude","SWEPT_EDGE",EDGE,{"disambiguationData":[OSD([subQ1,subQ0])]});Q87=makeQuery(id+"F16.opExtrude","CAP_EDGE",EDGE,{"disambiguationData":[OSD([subQ1,subQ0]),TDD([makeQuery(id+"F15.imprint","IMPRINT",EDGE,{"disambiguationData":[TD([[makeQuery(id+"F15.imprint","INTERSECT",VERTEX,{"derivedFrom":[subQ2,sQuery(id+"F15.wireOp",EDGE,"E112.right")]}),-1.0]])],"derivedFrom":subQ2})])],"isStart":false});}
            chamfer(context, id + "F17", {"entities" : qUnion([Q0, Q1, Q2, Q3, Q4, Q5, Q6, Q7, Q8, Q9, Q10, Q11, Q12, Q13, Q14, Q15, Q16, Q17, Q18, Q19, Q20, Q21, Q22, Q23, Q24, Q25, Q26, Q27, Q28, Q29, Q30, Q31, Q32, Q33, Q34, Q35, Q36, Q37, Q38, Q39, Q40, Q41, Q42, Q43, Q44, Q45, Q46, Q47, Q48, Q49, Q50, Q51, Q52, Q53, Q54, Q55, Q56, Q57, Q58, Q59, Q60, Q61, Q62, Q63, Q64, Q65, Q66, Q67, Q68, Q69, Q70, Q71, Q72, Q73, Q74, Q75, Q76, Q77, Q78, Q79, Q80, Q81, Q82, Q83, Q84, Q85, Q86, Q87]), "chamferType" : ChamferType.OFFSET_ANGLE, "width" : 2 * mm, "oppositeDirection" : false, "angle" : 60 * degree, "tangentPropagation" : true});
        }
        {
            var Q0;
            Q0=makeQuery(id+"F5.opExtrude","SWEPT_FACE",FACE,{"disambiguationData":[OSD([sQuery(id+"F4.wireOp",EDGE,"E38")])]});
            var sketch = newSketch(context, id + "F18", { "sketchPlane" : qUnion([Q0])});
            skLineSegment(sketch, "E163", {"start": v(20, 31.68) * mm, "end": v(29.55, 35.58) * mm});
            skLineSegment(sketch, "E164", {"start": v(29.55, 35.58) * mm, "end": v(49.94, -14.37) * mm});
            skLineSegment(sketch, "E165", {"start": v(49.94, -14.37) * mm, "end": v(43.53, -22.32) * mm});
            skLineSegment(sketch, "E166", {"start": v(43.53, -22.32) * mm, "end": v(20, -22.32) * mm});
            skSolve(sketch);
        }
        {
            var Q0;
            Q0=makeQuery(id+"F3.opExtrude","SWEPT_FACE",FACE,{"disambiguationData":[OSD([sQuery(id+"F2.wireOp",EDGE,"E18")])]});
            var sketch = newSketch(context, id + "F19", { "sketchPlane" : qUnion([Q0])});
            skLineSegment(sketch, "E167.bottom", {"start": v(-35, 74.62) * mm, "end": v(35, 74.62) * mm});
            skLineSegment(sketch, "E167.top", {"start": v(-35, 9.62) * mm, "end": v(35, 9.62) * mm});
            skLineSegment(sketch, "E167.left", {"start": v(-35, 74.62) * mm, "end": v(-35, 9.62) * mm});
            skLineSegment(sketch, "E167.right", {"start": v(35, 74.62) * mm, "end": v(35, 9.62) * mm});
            skPoint(sketch, "E167.middle", {"position": v(0, 42.12) * mm});
            skLineSegment(sketch, "E168.bottom", {"start": v(-59.11, 103.7) * mm, "end": v(-6.11, 103.7) * mm});
            skLineSegment(sketch, "E168.top", {"start": v(-59.11, 158.7) * mm, "end": v(-6.11, 158.7) * mm});
            skLineSegment(sketch, "E168.left", {"start": v(-59.11, 103.7) * mm, "end": v(-59.11, 158.7) * mm});
            skLineSegment(sketch, "E168.right", {"start": v(-6.11, 103.7) * mm, "end": v(-6.11, 158.7) * mm});
            skPoint(sketch, "E168.middle", {"position": v(-32.61, 131.2) * mm});
            skLineSegment(sketch, "E169.bottom", {"start": v(10.95, 103.7) * mm, "end": v(63.95, 103.7) * mm});
            skLineSegment(sketch, "E169.top", {"start": v(10.95, 158.7) * mm, "end": v(63.95, 158.7) * mm});
            skLineSegment(sketch, "E169.left", {"start": v(10.95, 103.7) * mm, "end": v(10.95, 158.7) * mm});
            skLineSegment(sketch, "E169.right", {"start": v(63.95, 103.7) * mm, "end": v(63.95, 158.7) * mm});
            skPoint(sketch, "E169.middle", {"position": v(37.45, 131.2) * mm});
            skSolve(sketch);
        }
        {
            var Q0;
            Q0=makeQuery(id+"F19.imprint","IMPRINT",FACE,{"disambiguationData":[TD([[makeQuery(id+"F19.imprint","IMPRINT",EDGE,{"derivedFrom":sQuery(id+"F19.wireOp",EDGE,"E167.bottom")}),-1.0]])]});
            var Q1;
            Q1=makeQuery(id+"F19.imprint","IMPRINT",FACE,{"disambiguationData":[TD([[makeQuery(id+"F19.imprint","IMPRINT",EDGE,{"derivedFrom":sQuery(id+"F19.wireOp",EDGE,"E169.bottom")}),1.0]])]});
            var Q2;
            Q2=makeQuery(id+"F19.imprint","IMPRINT",FACE,{"disambiguationData":[TD([[makeQuery(id+"F19.imprint","IMPRINT",EDGE,{"derivedFrom":sQuery(id+"F19.wireOp",EDGE,"E168.bottom")}),1.0]])]});
            extrude(context, id + "F20", {"entities" : qUnion([Q0, Q1, Q2]), "operationType" : NewBodyOperationType.ADD, "depth" : 50 * mm, "offsetDistance" : 25 * mm});
        }
        {
            var Q0;
            Q0=makeQuery(id+"F20.opExtrude","SWEPT_FACE",FACE,{"disambiguationData":[OSD([sQuery(id+"F19.wireOp",EDGE,"E167.top")])]});
            fillet(context, id + "F21", {"entities" : qUnion([Q0]), "radius" : 5 * mm, "tangentPropagation" : true, "allowEdgeOverflow" : false});
        }
        {
            var Q0;
            Q0=makeQuery(id+"F20.opExtrude","SWEPT_FACE",FACE,{"disambiguationData":[OSD([sQuery(id+"F19.wireOp",EDGE,"E168.bottom")])]});
            var Q1;
            Q1=makeQuery(id+"F20.opExtrude","SWEPT_FACE",FACE,{"disambiguationData":[OSD([sQuery(id+"F19.wireOp",EDGE,"E169.bottom")])]});
            fillet(context, id + "F22", {"entities" : qUnion([Q0, Q1]), "radius" : 3 * mm, "tangentPropagation" : true, "allowEdgeOverflow" : false});
        }
        {
            var Q0;
            Q0=makeQuery(id+"F18.imprint","IMPRINT",FACE,{"disambiguationData":[TD([[makeQuery(id+"F18.imprint","IMPRINT",EDGE,{"derivedFrom":sQuery(id+"F18.wireOp",EDGE,"E163")}),-1.0]])]});
            extrude(context, id + "F23", {"entities" : qUnion([Q0]), "oppositeDirection" : true, "depth" : 2 * mm, "offsetDistance" : 25 * mm});
        }
        {
            var Q0;
            Q0=makeQuery(id+"F23.opExtrude","CAP_FACE",FACE,{"disambiguationData":[OSD([sQuery(id+"F4.wireOp",EDGE,"E38"),sQuery(id+"F18.wireOp",EDGE,"E163"),sQuery(id+"F18.wireOp",EDGE,"E164"),sQuery(id+"F18.wireOp",EDGE,"E165"),sQuery(id+"F18.wireOp",EDGE,"E166")])],"isStart":false});
            var sketch = newSketch(context, id + "F24", { "sketchPlane" : qUnion([Q0])});
            skLineSegment(sketch, "E170", {"start": v(-20, 29.68) * mm, "end": v(-30.25, 33.86) * mm});
            skSolve(sketch);
        }
        {
            var Q0;
            {var subQ0=sQuery(id+"F24.wireOp",EDGE,"E170");Q0=makeQuery(id+"F24.imprint","IMPRINT",FACE,{"disambiguationData":[TD([[makeQuery(id+"F24.imprint","IMPRINT",EDGE,{"derivedFrom":subQ0}),-1.0]])]});}
            extrude(context, id + "F25", {"entities" : qUnion([Q0]), "depth" : 80 * mm, "offsetDistance" : 25 * mm});
        }
        {
            var Q0;
            Q0=makeQuery(id+"F23.opExtrude","CAP_FACE",FACE,{"disambiguationData":[OSD([sQuery(id+"F4.wireOp",EDGE,"E38"),sQuery(id+"F18.wireOp",EDGE,"E163"),sQuery(id+"F18.wireOp",EDGE,"E164"),sQuery(id+"F18.wireOp",EDGE,"E165"),sQuery(id+"F18.wireOp",EDGE,"E166")])],"isStart":false});
            var sketch = newSketch(context, id + "F26", { "sketchPlane" : qUnion([Q0])});
            skLineSegment(sketch, "E171", {"start": v(-20, -20.32) * mm, "end": v(-20.45, -20.32) * mm});
            skLineSegment(sketch, "E172", {"start": v(-20, -20.32) * mm, "end": v(-45.14, -20.32) * mm});
            skSolve(sketch);
        }
        {
            var Q0;
            {var subQ0=makeQuery(id+"F23.opExtrude","CAP_EDGE",EDGE,{"disambiguationData":[OSD([sQuery(id+"F18.wireOp",EDGE,"E166")])],"isStart":false});Q0=makeQuery(id+"F26.imprint","IMPRINT",FACE,{"disambiguationData":[TD([[makeQuery(id+"F26.imprint","IMPRINT",EDGE,{"derivedFrom":subQ0}),1.0]])]});}
            extrude(context, id + "F27", {"entities" : qUnion([Q0]), "depth" : 80 * mm, "offsetDistance" : 25 * mm});
        }
        {
            var Q0;
            Q0=makeQuery(id+"F5.opExtrude","SWEPT_FACE",FACE,{"disambiguationData":[OSD([sQuery(id+"F4.wireOp",EDGE,"E39")])]});
            var sketch = newSketch(context, id + "F28", { "sketchPlane" : qUnion([Q0])});
            skLineSegment(sketch, "E173.0.0", {"start": v(-43.53, -22.32) * mm, "end": v(-20, -22.32) * mm});
            skLineSegment(sketch, "E173.0.1", {"start": v(-20, -22.32) * mm, "end": v(-20, 31.68) * mm});
            skLineSegment(sketch, "E173.0.2", {"start": v(-20, 31.68) * mm, "end": v(-29.55, 35.58) * mm});
            skLineSegment(sketch, "E173.0.3", {"start": v(-29.55, 35.58) * mm, "end": v(-49.94, -14.37) * mm});
            skLineSegment(sketch, "E173.0.4", {"start": v(-49.94, -14.37) * mm, "end": v(-43.53, -22.32) * mm});
            skSolve(sketch);
        }
        {
            var Q0;
            Q0 = qSketchRegion(id + "F28", true);
            extrude(context, id + "F29", {"entities" : qUnion([Q0]), "oppositeDirection" : true, "depth" : 2 * mm, "offsetDistance" : 25 * mm});
        }
        {
            var Q0;
            Q0=makeQuery(id+"F23.opExtrude","CAP_FACE",FACE,{"disambiguationData":[OSD([sQuery(id+"F4.wireOp",EDGE,"E38"),sQuery(id+"F18.wireOp",EDGE,"E163"),sQuery(id+"F18.wireOp",EDGE,"E164"),sQuery(id+"F18.wireOp",EDGE,"E165"),sQuery(id+"F18.wireOp",EDGE,"E166")])],"isStart":false});
            var sketch = newSketch(context, id + "F30", { "sketchPlane" : qUnion([Q0])});
            skLineSegment(sketch, "E174", {"start": v(-42.9, -19.91) * mm, "end": v(-49.08, -12.25) * mm});
            skLineSegment(sketch, "E175", {"start": v(-48.67, -12.75) * mm, "end": v(-42.58, -20.32) * mm});
            skLineSegment(sketch, "E176", {"start": v(-42.28, -20.32) * mm, "end": v(-45.14, -20.32) * mm});
            skSolve(sketch);
        }
        {
            var Q0;
            {var subQ6=sQuery(id+"F30.wireOp",EDGE,"E174");Q0=makeQuery(id+"F30.imprint","IMPRINT",FACE,{"disambiguationData":[TD([[makeQuery(id+"F30.imprint","IMPRINT",EDGE,{"derivedFrom":subQ6}),1.0]])]});}
            extrude(context, id + "F31", {"entities" : qUnion([Q0]), "depth" : 80 * mm, "offsetDistance" : 25 * mm});
        }
        {
            var Q0;
            {var subQ6=sQuery(id+"F4.wireOp",EDGE,"E37");Q0=makeQuery(id+"F4.imprint","IMPRINT",FACE,{"disambiguationData":[TD([[makeQuery(id+"F4.imprint","IMPRINT",EDGE,{"derivedFrom":subQ6}),1.0]])]});}
            var sketch = newSketch(context, id + "F32", { "sketchPlane" : qUnion([Q0])});
            skCircle(sketch, "E177", {"center": v(-65.73, 17.1) * mm, "radius": 13 * mm});
            skCircle(sketch, "E178", {"center": v(-38, 50.22) * mm, "radius": 13 * mm});
            skCircle(sketch, "E179", {"center": v(0, 50.22) * mm, "radius": 13 * mm});
            skCircle(sketch, "E180", {"center": v(38, 50.22) * mm, "radius": 13 * mm});
            skCircle(sketch, "E181", {"center": v(62, 17.1) * mm, "radius": 13 * mm});
            skCircle(sketch, "E182", {"center": v(-65.73, -10.9) * mm, "radius": 9.5 * mm});
            skCircle(sketch, "E183", {"center": v(-65.73, -10.9) * mm, "radius": 5.75 * mm});
            skCircle(sketch, "E184", {"center": v(62, -10.9) * mm, "radius": 9.5 * mm});
            skCircle(sketch, "E185", {"center": v(62, -10.9) * mm, "radius": 5.75 * mm});
            skCircle(sketch, "E186", {"center": v(-65.73, 17.1) * mm, "radius": 5.75 * mm});
            skCircle(sketch, "E187", {"center": v(-38, 50.22) * mm, "radius": 5.75 * mm});
            skCircle(sketch, "E188", {"center": v(0, 50.22) * mm, "radius": 5.75 * mm});
            skCircle(sketch, "E189", {"center": v(38, 50.22) * mm, "radius": 5.75 * mm});
            skCircle(sketch, "E190", {"center": v(62, 17.1) * mm, "radius": 5.75 * mm});
            skLineSegment(sketch, "E191", {"start": v(0, 50.22) * mm, "end": v(0, 50.22) * mm});
            skLineSegment(sketch, "E192", {"start": v(-65.73, -10.9) * mm, "end": v(-65.73, -10.9) * mm});
            skLineSegment(sketch, "E193", {"start": v(62, 17.1) * mm, "end": v(62, 17.1) * mm});
            skSolve(sketch);
        }
        {
            var Q0;
            Q0=makeQuery(id+"F32.imprint","IMPRINT",FACE,{"disambiguationData":[TD([[makeQuery(id+"F32.imprint","IMPRINT",EDGE,{"derivedFrom":sQuery(id+"F32.wireOp",EDGE,"E177")}),1.0]])]});
            var Q1;
            Q1=makeQuery(id+"F32.imprint","IMPRINT",FACE,{"disambiguationData":[TD([[makeQuery(id+"F32.imprint","IMPRINT",EDGE,{"derivedFrom":sQuery(id+"F32.wireOp",EDGE,"E178")}),1.0]])]});
            var Q2;
            Q2=makeQuery(id+"F32.imprint","IMPRINT",FACE,{"disambiguationData":[TD([[makeQuery(id+"F32.imprint","IMPRINT",EDGE,{"derivedFrom":sQuery(id+"F32.wireOp",EDGE,"E179")}),1.0]])]});
            var Q3;
            Q3=makeQuery(id+"F32.imprint","IMPRINT",FACE,{"disambiguationData":[TD([[makeQuery(id+"F32.imprint","IMPRINT",EDGE,{"derivedFrom":sQuery(id+"F32.wireOp",EDGE,"E180")}),1.0]])]});
            var Q4;
            Q4=makeQuery(id+"F32.imprint","IMPRINT",FACE,{"disambiguationData":[TD([[makeQuery(id+"F32.imprint","IMPRINT",EDGE,{"derivedFrom":sQuery(id+"F32.wireOp",EDGE,"E177")}),-1.0]])]});
            extrude(context, id + "F33", {"entities" : qUnion([Q0, Q1, Q2, Q3, Q4]), "operationType" : NewBodyOperationType.REMOVE, "depth" : 2.5 * mm, "offsetDistance" : 25 * mm});
        }
        {
            var Q0;
            Q0=makeQuery(id+"F32.imprint","IMPRINT",FACE,{"disambiguationData":[TD([[makeQuery(id+"F32.imprint","IMPRINT",EDGE,{"derivedFrom":sQuery(id+"F32.wireOp",EDGE,"E177")}),1.0]])]});
            var Q1;
            Q1=makeQuery(id+"F32.imprint","IMPRINT",FACE,{"disambiguationData":[TD([[makeQuery(id+"F32.imprint","IMPRINT",EDGE,{"derivedFrom":sQuery(id+"F32.wireOp",EDGE,"E178")}),1.0]])]});
            var Q2;
            Q2=makeQuery(id+"F32.imprint","IMPRINT",FACE,{"disambiguationData":[TD([[makeQuery(id+"F32.imprint","IMPRINT",EDGE,{"derivedFrom":sQuery(id+"F32.wireOp",EDGE,"E179")}),1.0]])]});
            var Q3;
            Q3=makeQuery(id+"F32.imprint","IMPRINT",FACE,{"disambiguationData":[TD([[makeQuery(id+"F32.imprint","IMPRINT",EDGE,{"derivedFrom":sQuery(id+"F32.wireOp",EDGE,"E180")}),1.0]])]});
            var Q4;
            Q4=makeQuery(id+"F32.imprint","IMPRINT",FACE,{"disambiguationData":[TD([[makeQuery(id+"F32.imprint","IMPRINT",EDGE,{"derivedFrom":sQuery(id+"F32.wireOp",EDGE,"E181")}),1.0]])]});
            var Q5;
            Q5=makeQuery(id+"F32.imprint","IMPRINT",FACE,{"disambiguationData":[TD([[makeQuery(id+"F32.imprint","IMPRINT",EDGE,{"derivedFrom":sQuery(id+"F32.wireOp",EDGE,"E182")}),1.0]])]});
            var Q6;
            Q6=makeQuery(id+"F32.imprint","IMPRINT",FACE,{"disambiguationData":[TD([[makeQuery(id+"F32.imprint","IMPRINT",EDGE,{"derivedFrom":sQuery(id+"F32.wireOp",EDGE,"E184")}),1.0]])]});
            extrude(context, id + "F34", {"entities" : qUnion([Q0, Q1, Q2, Q3, Q4, Q5, Q6]), "operationType" : NewBodyOperationType.REMOVE, "oppositeDirection" : true, "depth" : 4 * mm, "offsetDistance" : 25 * mm});
        }
        {
            var Q0;
            Q0=makeQuery(id+"F32.imprint","IMPRINT",FACE,{"disambiguationData":[TD([[makeQuery(id+"F32.imprint","IMPRINT",EDGE,{"derivedFrom":sQuery(id+"F32.wireOp",EDGE,"E183")}),1.0]])]});
            var Q1;
            Q1=makeQuery(id+"F32.imprint","IMPRINT",FACE,{"disambiguationData":[TD([[makeQuery(id+"F32.imprint","IMPRINT",EDGE,{"derivedFrom":sQuery(id+"F32.wireOp",EDGE,"E185")}),1.0]])]});
            var Q2;
            Q2=makeQuery(id+"F32.imprint","IMPRINT",FACE,{"disambiguationData":[TD([[makeQuery(id+"F32.imprint","IMPRINT",EDGE,{"derivedFrom":sQuery(id+"F32.wireOp",EDGE,"E187")}),1.0]])]});
            var Q3;
            Q3=makeQuery(id+"F32.imprint","IMPRINT",FACE,{"disambiguationData":[TD([[makeQuery(id+"F32.imprint","IMPRINT",EDGE,{"derivedFrom":sQuery(id+"F32.wireOp",EDGE,"E188")}),1.0]])]});
            var Q4;
            Q4=makeQuery(id+"F32.imprint","IMPRINT",FACE,{"disambiguationData":[TD([[makeQuery(id+"F32.imprint","IMPRINT",EDGE,{"derivedFrom":sQuery(id+"F32.wireOp",EDGE,"E189")}),1.0]])]});
            var Q5;
            Q5=makeQuery(id+"F32.imprint","IMPRINT",FACE,{"disambiguationData":[TD([[makeQuery(id+"F32.imprint","IMPRINT",EDGE,{"derivedFrom":sQuery(id+"F32.wireOp",EDGE,"E190")}),1.0]])]});
            var Q6;
            Q6=makeQuery(id+"F32.imprint","IMPRINT",FACE,{"disambiguationData":[TD([[makeQuery(id+"F32.imprint","IMPRINT",EDGE,{"derivedFrom":sQuery(id+"F32.wireOp",EDGE,"E186")}),1.0]])]});
            extrude(context, id + "F35", {"entities" : qUnion([Q0, Q1, Q2, Q3, Q4, Q5, Q6]), "operationType" : NewBodyOperationType.REMOVE, "oppositeDirection" : true, "depth" : 10 * mm, "offsetDistance" : 25 * mm});
        }
        {
            var Q0;
            Q0=makeQuery(id+"F3.opExtrude","SWEPT_FACE",FACE,{"disambiguationData":[OSD([sQuery(id+"F2.wireOp",EDGE,"E25")])]});
            var sketch = newSketch(context, id + "F36", { "sketchPlane" : qUnion([Q0])});
            skText(sketch, "E194", { "text": "X\n", "fontName": "OpenSans-Bold.ttf"});
            const initialGuessF36  = {"E194": [-0.0606, -0.15557, 1, 0, 0.13]};
            skSetInitialGuess(sketch, initialGuessF36);
            skSolve(sketch);
        }
        {
            var Q0;
            Q0=makeQuery(id+"F36.imprint","IMPRINT",FACE,{"disambiguationData":[TD([[makeQuery(id+"F36.imprint","IMPRINT",EDGE,{"derivedFrom":sQuery(id+"F36.wireOp",EDGE,"E194.sketch_text.stroke-0")}),-1.0]])]});
            extrude(context, id + "F37", {"entities" : qUnion([Q0]), "operationType" : NewBodyOperationType.REMOVE, "oppositeDirection" : true, "depth" : 5 * mm, "offsetDistance" : 25 * mm});
        }
    });
